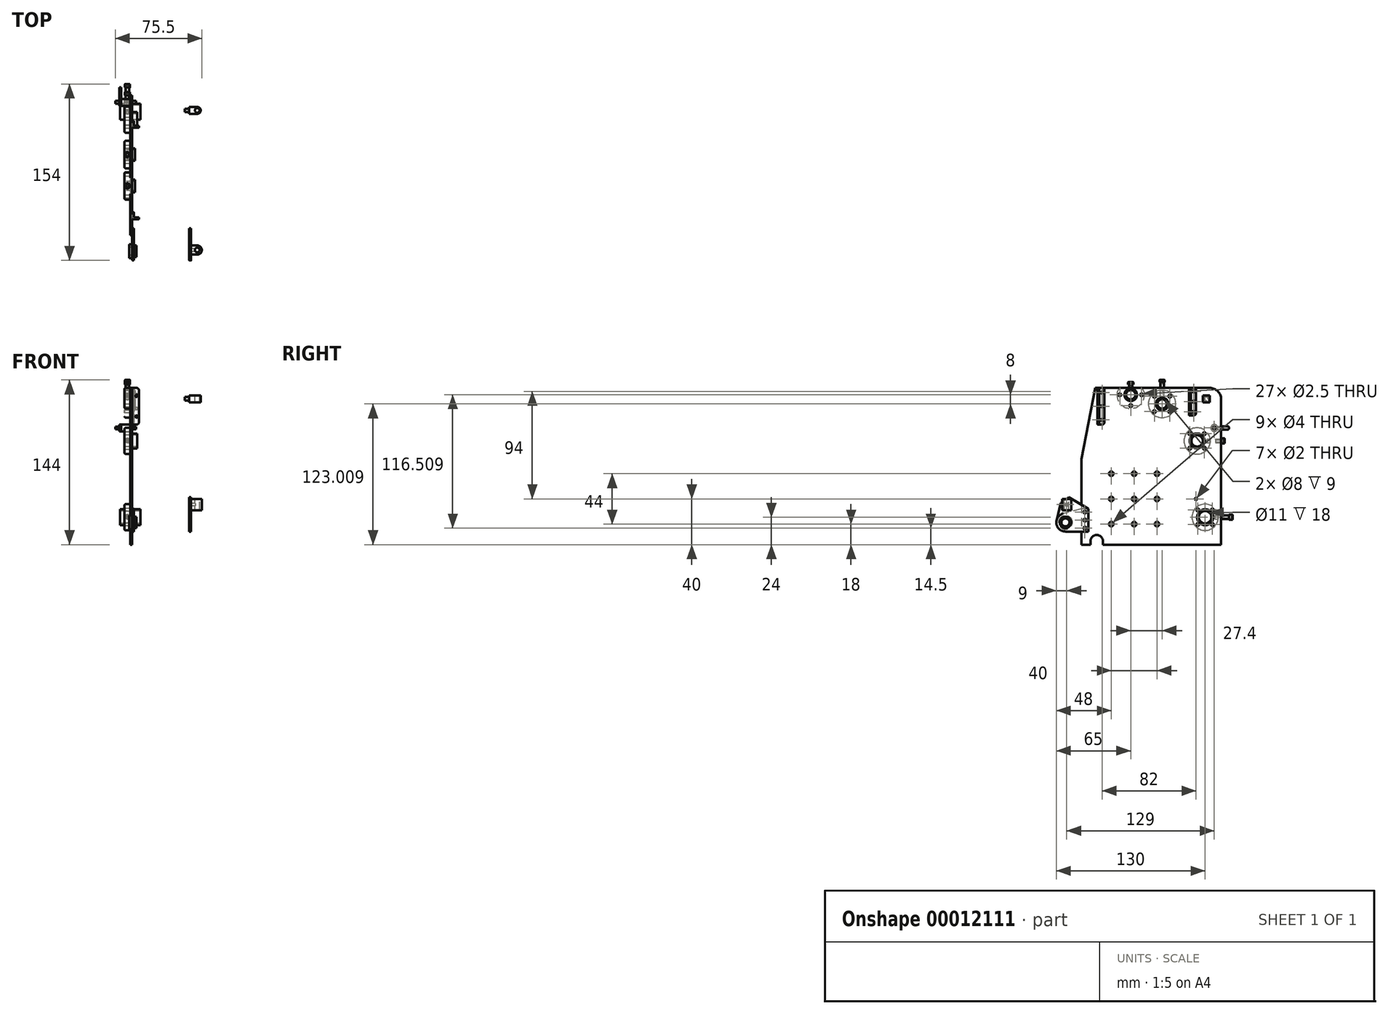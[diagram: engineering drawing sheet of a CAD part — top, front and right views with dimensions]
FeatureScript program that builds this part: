
annotation { "Feature Type Name" : "Feature", "Feature Type Description" : "" }
export const myFeature = defineFeature(function(context is Context, id is Id, definition is map)
    precondition{}
    {
        {
            var Q0;
            Q0=qCreatedBy(makeId("Right.planeOp"),FACE);
            var sketch = newSketch(context, id + "F0", { "sketchPlane" : qUnion([Q0])});
            skLineSegment(sketch, "E0", {"start": v(0, 75) * mm, "end": v(0, 0) * mm});
            skLineSegment(sketch, "E1", {"start": v(0, 0) * mm, "end": v(122, 0) * mm});
            skLineSegment(sketch, "E2", {"start": v(122, 0) * mm, "end": v(122, 127) * mm});
            skLineSegment(sketch, "E3", {"start": v(112, 137) * mm, "end": v(12, 137) * mm});
            skLineSegment(sketch, "E4", {"start": v(12, 137) * mm, "end": v(0, 75) * mm});
            skLineSegment(sketch, "E5", {"start": v(13.3, 0) * mm, "end": v(13.3, 3) * mm, "construction": true});
            skLineSegment(sketch, "E6", {"start": v(108, 0) * mm, "end": v(108, 24) * mm, "construction": true});
            skLineSegment(sketch, "E7", {"start": v(101, 0) * mm, "end": v(101, 90.7) * mm, "construction": true});
            skLineSegment(sketch, "E8", {"start": v(122, 40) * mm, "end": v(100, 40) * mm, "construction": true});
            skLineSegment(sketch, "E9", {"start": v(109, 137) * mm, "end": v(109, 127.5) * mm, "construction": true});
            skLineSegment(sketch, "E10", {"start": v(98, 137) * mm, "end": v(98, 134) * mm, "construction": true});
            skLineSegment(sketch, "E11", {"start": v(70.4, 137) * mm, "end": v(70.4, 101.73) * mm, "construction": true});
            skLineSegment(sketch, "E12", {"start": v(43, 137) * mm, "end": v(43, 131) * mm, "construction": true});
            skLineSegment(sketch, "E13", {"start": v(18, 137) * mm, "end": v(18, 133) * mm, "construction": true});
            skCircle(sketch, "E14", {"center": v(101, 90.7) * mm, "radius": 44.5 * mm, "construction": true});
            skCircle(sketch, "E15", {"center": v(70.4, 123) * mm, "radius": 5.5 * mm});
            skLineSegment(sketch, "E16", {"start": v(70.4, 123) * mm, "end": v(53.04, 123) * mm, "construction": true});
            skCircle(sketch, "E17", {"center": v(43, 131) * mm, "radius": 5.5 * mm});
            skCircle(sketch, "E18", {"center": v(101, 90.7) * mm, "radius": 6.5 * mm});
            skCircle(sketch, "E19", {"center": v(13.3, 3) * mm, "radius": 5.5 * mm});
            skCircle(sketch, "E20", {"center": v(108, 24) * mm, "radius": 7 * mm});
            skCircle(sketch, "E21", {"center": v(18, 133) * mm, "radius": 1 * mm});
            skCircle(sketch, "E22", {"center": v(98, 134) * mm, "radius": 1 * mm});
            skCircle(sketch, "E23", {"center": v(109, 127.5) * mm, "radius": 1.5 * mm});
            skCircle(sketch, "E24", {"center": v(100, 40) * mm, "radius": 1 * mm});
            skCircle(sketch, "E25.0.1.0", {"center": v(18, 121) * mm, "radius": 1 * mm});
            skCircle(sketch, "E25.0.2.0", {"center": v(18, 109) * mm, "radius": 1 * mm});
            skLineSegment(sketch, "E25.direction1", {"start": v(18, 133) * mm, "end": v(6, 133) * mm, "construction": true});
            skLineSegment(sketch, "E25.direction2", {"start": v(18, 133) * mm, "end": v(18, 121) * mm, "construction": true});
            skCircle(sketch, "E26.0.1.0", {"center": v(98, 125) * mm, "radius": 1 * mm});
            skCircle(sketch, "E26.0.2.0", {"center": v(98, 116) * mm, "radius": 1 * mm});
            skLineSegment(sketch, "E26.direction1", {"start": v(98, 134) * mm, "end": v(123, 134) * mm, "construction": true});
            skLineSegment(sketch, "E26.direction2", {"start": v(98, 134) * mm, "end": v(98, 125) * mm, "construction": true});
            skLineSegment(sketch, "E27", {"start": v(122, 102) * mm, "end": v(116, 102) * mm, "construction": true});
            skCircle(sketch, "E28", {"center": v(116, 102) * mm, "radius": 1.25 * mm});
            skLineSegment(sketch, "E29", {"start": v(43, 131) * mm, "end": v(33.5, 131) * mm, "construction": true});
            skCircle(sketch, "E30", {"center": v(33.5, 131) * mm, "radius": 1.25 * mm});
            skLineSegment(sketch, "E31", {"start": v(70.4, 123) * mm, "end": v(63.68, 129.73) * mm, "construction": true});
            skCircle(sketch, "E32", {"center": v(63.68, 129.73) * mm, "radius": 1.25 * mm});
            skCircle(sketch, "E33.1.0", {"center": v(63.68, 116.3) * mm, "radius": 1.25 * mm});
            skCircle(sketch, "E33.2.0", {"center": v(77.12, 116.3) * mm, "radius": 1.25 * mm});
            skCircle(sketch, "E33.3.0", {"center": v(77.12, 129.73) * mm, "radius": 1.25 * mm});
            skLineSegment(sketch, "E34", {"start": v(101, 90.7) * mm, "end": v(94.64, 84.34) * mm, "construction": true});
            skCircle(sketch, "E35", {"center": v(94.64, 84.34) * mm, "radius": 1.25 * mm});
            skCircle(sketch, "E36.1.0", {"center": v(107.36, 84.34) * mm, "radius": 1.25 * mm});
            skCircle(sketch, "E36.2.0", {"center": v(107.36, 97.06) * mm, "radius": 1.25 * mm});
            skCircle(sketch, "E36.3.0", {"center": v(94.64, 97.06) * mm, "radius": 1.25 * mm});
            skLineSegment(sketch, "E37", {"start": v(108, 24) * mm, "end": v(114.36, 17.64) * mm, "construction": true});
            skCircle(sketch, "E38", {"center": v(114.36, 17.64) * mm, "radius": 1.25 * mm});
            skCircle(sketch, "E39.1.0", {"center": v(114.36, 30.36) * mm, "radius": 1.25 * mm});
            skCircle(sketch, "E39.2.0", {"center": v(101.64, 30.36) * mm, "radius": 1.25 * mm});
            skCircle(sketch, "E39.3.0", {"center": v(101.64, 17.64) * mm, "radius": 1.25 * mm});
            skLineSegment(sketch, "E40", {"start": v(7.8, 3) * mm, "end": v(7.8, 0) * mm});
            skLineSegment(sketch, "E41", {"start": v(18.8, 3) * mm, "end": v(18.8, 0) * mm});
            skLineSegment(sketch, "E42", {"start": v(66, 0) * mm, "end": v(66, 18) * mm, "construction": true});
            skCircle(sketch, "E43", {"center": v(66, 18) * mm, "radius": 2 * mm});
            skCircle(sketch, "E44.0.1.0", {"center": v(66, 40) * mm, "radius": 2 * mm});
            skCircle(sketch, "E44.0.2.0", {"center": v(66, 62) * mm, "radius": 2 * mm});
            skCircle(sketch, "E44.1.0.0", {"center": v(46, 18) * mm, "radius": 2 * mm});
            skCircle(sketch, "E44.1.1.0", {"center": v(46, 40) * mm, "radius": 2 * mm});
            skCircle(sketch, "E44.1.2.0", {"center": v(46, 62) * mm, "radius": 2 * mm});
            skCircle(sketch, "E44.2.0.0", {"center": v(26, 18) * mm, "radius": 2 * mm});
            skCircle(sketch, "E44.2.1.0", {"center": v(26, 40) * mm, "radius": 2 * mm});
            skCircle(sketch, "E44.2.2.0", {"center": v(26, 62) * mm, "radius": 2 * mm});
            skLineSegment(sketch, "E44.direction1", {"start": v(66, 18) * mm, "end": v(46, 18) * mm, "construction": true});
            skLineSegment(sketch, "E44.direction2", {"start": v(66, 18) * mm, "end": v(66, 40) * mm, "construction": true});
            skLineSegment(sketch, "E45", {"start": v(0, 14.5) * mm, "end": v(3, 14.5) * mm, "construction": true});
            skCircle(sketch, "E46", {"center": v(3, 14.5) * mm, "radius": 1.25 * mm});
            skCircle(sketch, "E47.0.1.0", {"center": v(3, 21.5) * mm, "radius": 1.25 * mm});
            skCircle(sketch, "E47.0.2.0", {"center": v(3, 28.5) * mm, "radius": 1.25 * mm});
            skLineSegment(sketch, "E47.direction1", {"start": v(3, 14.5) * mm, "end": v(3, 14.5) * mm});
            skLineSegment(sketch, "E47.direction2", {"start": v(3, 14.5) * mm, "end": v(3, 21.5) * mm, "construction": true});
            skPoint(sketch, "E48.visualSharp", {"position": v(122, 137) * mm});
            skArc(sketch, "E48.filletArc", {"start": v(122, 127) * mm, "mid": v(119.07, 134.07) * mm, "end": v(112, 137) * mm});
            skCircle(sketch, "E49.1.0", {"center": v(43, 121.5) * mm, "radius": 1.25 * mm});
            skCircle(sketch, "E49.2.0", {"center": v(52.5, 131) * mm, "radius": 1.25 * mm});
            skCircle(sketch, "E49.3.0", {"center": v(43, 140.5) * mm, "radius": 1.25 * mm});
            skSolve(sketch);
        }
        {
            var Q0;
            {var subQ2=sQuery(id+"F0.wireOp",EDGE,"E0");Q0=makeQuery(id+"F0.imprint","IMPRINT",FACE,{"disambiguationData":[TD([[makeQuery(id+"F0.imprint","IMPRINT",EDGE,{"derivedFrom":subQ2}),1.0]])]});}
            extrude(context, id + "F1", {"entities" : qUnion([Q0]), "depth" : 1.5 * mm});
        }
        {
            var Q0;
            Q0=makeQuery(id+"F1.opExtrude","CAP_FACE",FACE,{"disambiguationData":[OSD([sQuery(id+"F0.wireOp",EDGE,"E0"),sQuery(id+"F0.wireOp",EDGE,"E1"),sQuery(id+"F0.wireOp",EDGE,"E2"),sQuery(id+"F0.wireOp",EDGE,"E3"),sQuery(id+"F0.wireOp",EDGE,"E4"),sQuery(id+"F0.wireOp",EDGE,"E15"),sQuery(id+"F0.wireOp",EDGE,"E17"),sQuery(id+"F0.wireOp",EDGE,"E18"),sQuery(id+"F0.wireOp",EDGE,"E19"),sQuery(id+"F0.wireOp",EDGE,"E20"),sQuery(id+"F0.wireOp",EDGE,"E21"),sQuery(id+"F0.wireOp",EDGE,"E22"),sQuery(id+"F0.wireOp",EDGE,"E23"),sQuery(id+"F0.wireOp",EDGE,"E24"),sQuery(id+"F0.wireOp",EDGE,"E25.0.1.0"),sQuery(id+"F0.wireOp",EDGE,"E25.0.2.0"),sQuery(id+"F0.wireOp",EDGE,"E26.0.1.0"),sQuery(id+"F0.wireOp",EDGE,"E26.0.2.0"),sQuery(id+"F0.wireOp",EDGE,"E28"),sQuery(id+"F0.wireOp",EDGE,"E30"),sQuery(id+"F0.wireOp",EDGE,"E32"),sQuery(id+"F0.wireOp",EDGE,"E33.1.0"),sQuery(id+"F0.wireOp",EDGE,"E33.2.0"),sQuery(id+"F0.wireOp",EDGE,"E33.3.0"),sQuery(id+"F0.wireOp",EDGE,"E35"),sQuery(id+"F0.wireOp",EDGE,"E36.1.0"),sQuery(id+"F0.wireOp",EDGE,"E36.2.0"),sQuery(id+"F0.wireOp",EDGE,"E36.3.0"),sQuery(id+"F0.wireOp",EDGE,"E38"),sQuery(id+"F0.wireOp",EDGE,"E39.1.0"),sQuery(id+"F0.wireOp",EDGE,"E39.2.0"),sQuery(id+"F0.wireOp",EDGE,"E39.3.0"),sQuery(id+"F0.wireOp",EDGE,"E40"),sQuery(id+"F0.wireOp",EDGE,"E41"),sQuery(id+"F0.wireOp",EDGE,"E43"),sQuery(id+"F0.wireOp",EDGE,"E44.0.1.0"),sQuery(id+"F0.wireOp",EDGE,"E44.0.2.0"),sQuery(id+"F0.wireOp",EDGE,"E44.1.0.0"),sQuery(id+"F0.wireOp",EDGE,"E44.1.1.0"),sQuery(id+"F0.wireOp",EDGE,"E44.1.2.0"),sQuery(id+"F0.wireOp",EDGE,"E44.2.0.0"),sQuery(id+"F0.wireOp",EDGE,"E44.2.1.0"),sQuery(id+"F0.wireOp",EDGE,"E44.2.2.0"),sQuery(id+"F0.wireOp",EDGE,"E46"),sQuery(id+"F0.wireOp",EDGE,"E47.0.1.0"),sQuery(id+"F0.wireOp",EDGE,"E47.0.2.0"),sQuery(id+"F0.wireOp",EDGE,"E48.filletArc"),sQuery(id+"F0.wireOp",EDGE,"E49.1.0"),sQuery(id+"F0.wireOp",EDGE,"E49.2.0")])],"isStart":false});
            var sketch = newSketch(context, id + "F2", { "sketchPlane" : qUnion([Q0])});
            skCircle(sketch, "E50.0", {"center": v(18, 133) * mm, "radius": 1 * mm});
            skCircle(sketch, "E50.1", {"center": v(18, 121) * mm, "radius": 1 * mm});
            skCircle(sketch, "E50.2", {"center": v(18, 109) * mm, "radius": 1 * mm});
            skLineSegment(sketch, "E51.bottom", {"start": v(14, 137) * mm, "end": v(18, 137) * mm});
            skLineSegment(sketch, "E51.top", {"start": v(14, 105) * mm, "end": v(18, 105) * mm});
            skLineSegment(sketch, "E51.left", {"start": v(14, 137) * mm, "end": v(14, 105) * mm});
            skLineSegment(sketch, "E51.right", {"start": v(20, 135) * mm, "end": v(20, 107) * mm});
            skLineSegment(sketch, "E52", {"start": v(15.5, 137) * mm, "end": v(15.5, 105) * mm});
            skPoint(sketch, "E53.visualSharp", {"position": v(20, 137) * mm});
            skArc(sketch, "E53.filletArc", {"start": v(20, 135) * mm, "mid": v(19.41, 136.41) * mm, "end": v(18, 137) * mm});
            skPoint(sketch, "E54.visualSharp", {"position": v(20, 105) * mm});
            skArc(sketch, "E54.filletArc", {"start": v(18, 105) * mm, "mid": v(19.41, 105.59) * mm, "end": v(20, 107) * mm});
            skSolve(sketch);
        }
        {
            var Q0;
            {var subQ1=sQuery(id+"F2.wireOp",EDGE,"E51.left");Q0=makeQuery(id+"F2.imprint","IMPRINT",FACE,{"disambiguationData":[TD([[makeQuery(id+"F2.imprint","IMPRINT",EDGE,{"derivedFrom":subQ1}),1.0]])]});}
            extrude(context, id + "F3", {"entities" : qUnion([Q0]), "depth" : 6 * mm});
        }
        {
            var Q0;
            Q0=makeQuery(id+"F2.imprint","IMPRINT",FACE,{"disambiguationData":[TD([[makeQuery(id+"F2.imprint","IMPRINT",EDGE,{"derivedFrom":sQuery(id+"F2.wireOp",EDGE,"E50.0")}),-1.0]])]});
            extrude(context, id + "F4", {"entities" : qUnion([Q0]), "operationType" : NewBodyOperationType.ADD, "depth" : 1.5 * mm});
        }
        {
            var Q0;
            Q0=makeQuery(id+"F3.opExtrude","SWEPT_FACE",FACE,{"disambiguationData":[OSD([sQuery(id+"F2.wireOp",EDGE,"E51.left")])]});
            var sketch = newSketch(context, id + "F5", { "sketchPlane" : qUnion([Q0])});
            skLineSegment(sketch, "E55", {"start": v(5.5, 137) * mm, "end": v(5.5, 105) * mm, "construction": true});
            skLineSegment(sketch, "E56", {"start": v(5.5, 130) * mm, "end": v(7.5, 130) * mm, "construction": true});
            skLineSegment(sketch, "E57", {"start": v(5.5, 112) * mm, "end": v(7.5, 112) * mm, "construction": true});
            skCircle(sketch, "E58", {"center": v(5.5, 130) * mm, "radius": 1 * mm});
            skCircle(sketch, "E59", {"center": v(5.5, 112) * mm, "radius": 1 * mm});
            skSolve(sketch);
        }
        {
            var Q0;
            Q0=makeQuery(id+"F5.imprint","IMPRINT",FACE,{"disambiguationData":[TD([[makeQuery(id+"F5.imprint","IMPRINT",EDGE,{"derivedFrom":sQuery(id+"F5.wireOp",EDGE,"E58")}),1.0]])]});
            var Q1;
            Q1=makeQuery(id+"F5.imprint","IMPRINT",FACE,{"disambiguationData":[TD([[makeQuery(id+"F5.imprint","IMPRINT",EDGE,{"derivedFrom":sQuery(id+"F5.wireOp",EDGE,"E59")}),1.0]])]});
            extrude(context, id + "F6", {"entities" : qUnion([Q0, Q1]), "operationType" : NewBodyOperationType.REMOVE, "oppositeDirection" : true, "depth" : 1.5 * mm});
        }
        {
            var Q0;
            Q0=makeQuery(id+"F3.opExtrude","CAP_EDGE",EDGE,{"disambiguationData":[OSD([sQuery(id+"F2.wireOp",EDGE,"E51.bottom")])],"isStart":false});
            var Q1;
            Q1=makeQuery(id+"F3.opExtrude","CAP_EDGE",EDGE,{"disambiguationData":[OSD([sQuery(id+"F2.wireOp",EDGE,"E51.top")])],"isStart":false});
            fillet(context, id + "F7", {"entities" : qUnion([Q0, Q1]), "radius" : 2 * mm, "tangentPropagation" : true, "allowEdgeOverflow" : false});
        }
        {
            var Q0;
            Q0=makeQuery(id+"F1.opExtrude","CAP_FACE",FACE,{"disambiguationData":[OSD([sQuery(id+"F0.wireOp",EDGE,"E0"),sQuery(id+"F0.wireOp",EDGE,"E1"),sQuery(id+"F0.wireOp",EDGE,"E2"),sQuery(id+"F0.wireOp",EDGE,"E3"),sQuery(id+"F0.wireOp",EDGE,"E4"),sQuery(id+"F0.wireOp",EDGE,"E15"),sQuery(id+"F0.wireOp",EDGE,"E17"),sQuery(id+"F0.wireOp",EDGE,"E18"),sQuery(id+"F0.wireOp",EDGE,"E19"),sQuery(id+"F0.wireOp",EDGE,"E20"),sQuery(id+"F0.wireOp",EDGE,"E21"),sQuery(id+"F0.wireOp",EDGE,"E22"),sQuery(id+"F0.wireOp",EDGE,"E23"),sQuery(id+"F0.wireOp",EDGE,"E24"),sQuery(id+"F0.wireOp",EDGE,"E25.0.1.0"),sQuery(id+"F0.wireOp",EDGE,"E25.0.2.0"),sQuery(id+"F0.wireOp",EDGE,"E26.0.1.0"),sQuery(id+"F0.wireOp",EDGE,"E26.0.2.0"),sQuery(id+"F0.wireOp",EDGE,"E28"),sQuery(id+"F0.wireOp",EDGE,"E30"),sQuery(id+"F0.wireOp",EDGE,"E32"),sQuery(id+"F0.wireOp",EDGE,"E33.1.0"),sQuery(id+"F0.wireOp",EDGE,"E33.2.0"),sQuery(id+"F0.wireOp",EDGE,"E33.3.0"),sQuery(id+"F0.wireOp",EDGE,"E35"),sQuery(id+"F0.wireOp",EDGE,"E36.1.0"),sQuery(id+"F0.wireOp",EDGE,"E36.2.0"),sQuery(id+"F0.wireOp",EDGE,"E36.3.0"),sQuery(id+"F0.wireOp",EDGE,"E38"),sQuery(id+"F0.wireOp",EDGE,"E39.1.0"),sQuery(id+"F0.wireOp",EDGE,"E39.2.0"),sQuery(id+"F0.wireOp",EDGE,"E39.3.0"),sQuery(id+"F0.wireOp",EDGE,"E40"),sQuery(id+"F0.wireOp",EDGE,"E41"),sQuery(id+"F0.wireOp",EDGE,"E43"),sQuery(id+"F0.wireOp",EDGE,"E44.0.1.0"),sQuery(id+"F0.wireOp",EDGE,"E44.0.2.0"),sQuery(id+"F0.wireOp",EDGE,"E44.1.0.0"),sQuery(id+"F0.wireOp",EDGE,"E44.1.1.0"),sQuery(id+"F0.wireOp",EDGE,"E44.1.2.0"),sQuery(id+"F0.wireOp",EDGE,"E44.2.0.0"),sQuery(id+"F0.wireOp",EDGE,"E44.2.1.0"),sQuery(id+"F0.wireOp",EDGE,"E44.2.2.0"),sQuery(id+"F0.wireOp",EDGE,"E46"),sQuery(id+"F0.wireOp",EDGE,"E47.0.1.0"),sQuery(id+"F0.wireOp",EDGE,"E47.0.2.0"),sQuery(id+"F0.wireOp",EDGE,"E48.filletArc"),sQuery(id+"F0.wireOp",EDGE,"E49.1.0"),sQuery(id+"F0.wireOp",EDGE,"E49.2.0")])],"isStart":false});
            var sketch = newSketch(context, id + "F8", { "sketchPlane" : qUnion([Q0])});
            skCircle(sketch, "E60.0", {"center": v(98, 134) * mm, "radius": 1 * mm});
            skCircle(sketch, "E60.1", {"center": v(98, 125) * mm, "radius": 1 * mm});
            skCircle(sketch, "E60.2", {"center": v(98, 116) * mm, "radius": 1 * mm});
            skLineSegment(sketch, "E61.bottom", {"start": v(98, 137) * mm, "end": v(94, 137) * mm});
            skLineSegment(sketch, "E61.top", {"start": v(98, 113) * mm, "end": v(94, 113) * mm});
            skLineSegment(sketch, "E61.left", {"start": v(100, 135) * mm, "end": v(100, 115) * mm});
            skLineSegment(sketch, "E61.right", {"start": v(94, 137) * mm, "end": v(94, 113) * mm});
            skLineSegment(sketch, "E62", {"start": v(95.5, 137) * mm, "end": v(95.5, 113) * mm});
            skPoint(sketch, "E63.visualSharp", {"position": v(100, 113) * mm});
            skArc(sketch, "E63.filletArc", {"start": v(98, 113) * mm, "mid": v(99.41, 113.59) * mm, "end": v(100, 115) * mm});
            skPoint(sketch, "E64.visualSharp", {"position": v(100, 137) * mm});
            skArc(sketch, "E64.filletArc", {"start": v(100, 135) * mm, "mid": v(99.41, 136.41) * mm, "end": v(98, 137) * mm});
            skSolve(sketch);
        }
        {
            var Q0;
            {var subQ1=sQuery(id+"F8.wireOp",EDGE,"E61.right");Q0=makeQuery(id+"F8.imprint","IMPRINT",FACE,{"disambiguationData":[TD([[makeQuery(id+"F8.imprint","IMPRINT",EDGE,{"derivedFrom":subQ1}),1.0]])]});}
            extrude(context, id + "F9", {"entities" : qUnion([Q0]), "depth" : 6 * mm});
        }
        {
            var Q0;
            Q0=makeQuery(id+"F8.imprint","IMPRINT",FACE,{"disambiguationData":[TD([[makeQuery(id+"F8.imprint","IMPRINT",EDGE,{"derivedFrom":sQuery(id+"F8.wireOp",EDGE,"E60.0")}),-1.0]])]});
            extrude(context, id + "F10", {"entities" : qUnion([Q0]), "operationType" : NewBodyOperationType.ADD, "depth" : 1.5 * mm});
        }
        {
            var Q0;
            Q0=makeQuery(id+"F9.opExtrude","SWEPT_FACE",FACE,{"disambiguationData":[OSD([sQuery(id+"F8.wireOp",EDGE,"E61.right")])]});
            var sketch = newSketch(context, id + "F11", { "sketchPlane" : qUnion([Q0])});
            skLineSegment(sketch, "E65", {"start": v(5.5, 137) * mm, "end": v(5.5, 113) * mm, "construction": true});
            skLineSegment(sketch, "E66", {"start": v(5.5, 131) * mm, "end": v(7.5, 131) * mm, "construction": true});
            skLineSegment(sketch, "E67", {"start": v(5.5, 119) * mm, "end": v(7.5, 119) * mm, "construction": true});
            skCircle(sketch, "E68", {"center": v(5.5, 131) * mm, "radius": 1 * mm});
            skCircle(sketch, "E69", {"center": v(5.5, 119) * mm, "radius": 1 * mm});
            skSolve(sketch);
        }
        {
            var Q0;
            Q0=makeQuery(id+"F11.imprint","IMPRINT",FACE,{"disambiguationData":[TD([[makeQuery(id+"F11.imprint","IMPRINT",EDGE,{"derivedFrom":sQuery(id+"F11.wireOp",EDGE,"E68")}),1.0]])]});
            var Q1;
            Q1=makeQuery(id+"F11.imprint","IMPRINT",FACE,{"disambiguationData":[TD([[makeQuery(id+"F11.imprint","IMPRINT",EDGE,{"derivedFrom":sQuery(id+"F11.wireOp",EDGE,"E69")}),1.0]])]});
            extrude(context, id + "F12", {"entities" : qUnion([Q0, Q1]), "operationType" : NewBodyOperationType.REMOVE, "oppositeDirection" : true, "depth" : 1.5 * mm});
        }
        {
            var Q0;
            Q0=makeQuery(id+"F9.opExtrude","CAP_EDGE",EDGE,{"disambiguationData":[OSD([sQuery(id+"F8.wireOp",EDGE,"E61.bottom")])],"isStart":false});
            var Q1;
            Q1=makeQuery(id+"F9.opExtrude","CAP_EDGE",EDGE,{"disambiguationData":[OSD([sQuery(id+"F8.wireOp",EDGE,"E61.top")])],"isStart":false});
            fillet(context, id + "F13", {"entities" : qUnion([Q0, Q1]), "radius" : 2 * mm, "tangentPropagation" : true, "allowEdgeOverflow" : false});
        }
        {
            var Q0;
            Q0=makeQuery(id+"F1.opExtrude","CAP_FACE",FACE,{"disambiguationData":[OSD([sQuery(id+"F0.wireOp",EDGE,"E0"),sQuery(id+"F0.wireOp",EDGE,"E1"),sQuery(id+"F0.wireOp",EDGE,"E2"),sQuery(id+"F0.wireOp",EDGE,"E3"),sQuery(id+"F0.wireOp",EDGE,"E4"),sQuery(id+"F0.wireOp",EDGE,"E15"),sQuery(id+"F0.wireOp",EDGE,"E17"),sQuery(id+"F0.wireOp",EDGE,"E18"),sQuery(id+"F0.wireOp",EDGE,"E19"),sQuery(id+"F0.wireOp",EDGE,"E20"),sQuery(id+"F0.wireOp",EDGE,"E21"),sQuery(id+"F0.wireOp",EDGE,"E22"),sQuery(id+"F0.wireOp",EDGE,"E23"),sQuery(id+"F0.wireOp",EDGE,"E24"),sQuery(id+"F0.wireOp",EDGE,"E25.0.1.0"),sQuery(id+"F0.wireOp",EDGE,"E25.0.2.0"),sQuery(id+"F0.wireOp",EDGE,"E26.0.1.0"),sQuery(id+"F0.wireOp",EDGE,"E26.0.2.0"),sQuery(id+"F0.wireOp",EDGE,"E28"),sQuery(id+"F0.wireOp",EDGE,"E30"),sQuery(id+"F0.wireOp",EDGE,"E32"),sQuery(id+"F0.wireOp",EDGE,"E33.1.0"),sQuery(id+"F0.wireOp",EDGE,"E33.2.0"),sQuery(id+"F0.wireOp",EDGE,"E33.3.0"),sQuery(id+"F0.wireOp",EDGE,"E35"),sQuery(id+"F0.wireOp",EDGE,"E36.1.0"),sQuery(id+"F0.wireOp",EDGE,"E36.2.0"),sQuery(id+"F0.wireOp",EDGE,"E36.3.0"),sQuery(id+"F0.wireOp",EDGE,"E38"),sQuery(id+"F0.wireOp",EDGE,"E39.1.0"),sQuery(id+"F0.wireOp",EDGE,"E39.2.0"),sQuery(id+"F0.wireOp",EDGE,"E39.3.0"),sQuery(id+"F0.wireOp",EDGE,"E40"),sQuery(id+"F0.wireOp",EDGE,"E41"),sQuery(id+"F0.wireOp",EDGE,"E43"),sQuery(id+"F0.wireOp",EDGE,"E44.0.1.0"),sQuery(id+"F0.wireOp",EDGE,"E44.0.2.0"),sQuery(id+"F0.wireOp",EDGE,"E44.1.0.0"),sQuery(id+"F0.wireOp",EDGE,"E44.1.1.0"),sQuery(id+"F0.wireOp",EDGE,"E44.1.2.0"),sQuery(id+"F0.wireOp",EDGE,"E44.2.0.0"),sQuery(id+"F0.wireOp",EDGE,"E44.2.1.0"),sQuery(id+"F0.wireOp",EDGE,"E44.2.2.0"),sQuery(id+"F0.wireOp",EDGE,"E46"),sQuery(id+"F0.wireOp",EDGE,"E47.0.1.0"),sQuery(id+"F0.wireOp",EDGE,"E47.0.2.0"),sQuery(id+"F0.wireOp",EDGE,"E48.filletArc"),sQuery(id+"F0.wireOp",EDGE,"E49.1.0"),sQuery(id+"F0.wireOp",EDGE,"E49.2.0")])],"isStart":true});
            var sketch = newSketch(context, id + "F14", { "sketchPlane" : qUnion([Q0])});
            skCircle(sketch, "E70.0", {"center": v(-43, 131) * mm, "radius": 5.5 * mm});
            skCircle(sketch, "E70.1", {"center": v(-43, 121.5) * mm, "radius": 1.25 * mm});
            skCircle(sketch, "E70.2", {"center": v(-52.5, 131) * mm, "radius": 1.25 * mm});
            skCircle(sketch, "E70.3", {"center": v(-33.5, 131) * mm, "radius": 1.25 * mm});
            skCircle(sketch, "E71", {"center": v(-43, 131) * mm, "radius": 12 * mm});
            skCircle(sketch, "E72", {"center": v(-43, 131) * mm, "radius": 4 * mm});
            skSolve(sketch);
        }
        {
            var Q0;
            Q0=makeQuery(id+"F14.imprint","IMPRINT",FACE,{"disambiguationData":[TD([[makeQuery(id+"F14.imprint","IMPRINT",EDGE,{"derivedFrom":sQuery(id+"F14.wireOp",EDGE,"E70.0")}),-1.0]])]});
            extrude(context, id + "F15", {"entities" : qUnion([Q0]), "oppositeDirection" : true, "depth" : 4 * mm});
        }
        {
            var Q0;
            Q0=makeQuery(id+"F14.imprint","IMPRINT",FACE,{"disambiguationData":[TD([[makeQuery(id+"F14.imprint","IMPRINT",EDGE,{"derivedFrom":sQuery(id+"F14.wireOp",EDGE,"E70.0")}),1.0]])]});
            var Q1;
            Q1=makeQuery(id+"F14.imprint","IMPRINT",FACE,{"disambiguationData":[TD([[makeQuery(id+"F14.imprint","IMPRINT",EDGE,{"derivedFrom":sQuery(id+"F14.wireOp",EDGE,"E70.0")}),-1.0]])]});
            extrude(context, id + "F16", {"entities" : qUnion([Q0, Q1]), "operationType" : NewBodyOperationType.ADD, "depth" : 5 * mm});
        }
        {
            var Q0;
            Q0=makeQuery(id+"F16.opExtrude","SWEPT_FACE",FACE,{"disambiguationData":[OSD([sQuery(id+"F0.wireOp",EDGE,"E3")])]});
            var sketch = newSketch(context, id + "F17", { "sketchPlane" : qUnion([Q0])});
            skLineSegment(sketch, "E73", {"start": v(-5, 43) * mm, "end": v(0, 43) * mm, "construction": true});
            skCircle(sketch, "E74", {"center": v(-2.5, 43) * mm, "radius": 1.5 * mm});
            skCircle(sketch, "E75", {"center": v(-2.5, 43) * mm, "radius": 0.75 * mm});
            skSolve(sketch);
        }
        {
            var Q0;
            Q0=makeQuery(id+"F17.imprint","IMPRINT",FACE,{"disambiguationData":[TD([[makeQuery(id+"F17.imprint","IMPRINT",EDGE,{"derivedFrom":sQuery(id+"F17.wireOp",EDGE,"E75")}),1.0]])]});
            extrude(context, id + "F18", {"entities" : qUnion([Q0]), "operationType" : NewBodyOperationType.REMOVE, "oppositeDirection" : true, "depth" : 6 * mm});
        }
        {
            var Q0;
            Q0=makeQuery(id+"F17.imprint","IMPRINT",FACE,{"disambiguationData":[TD([[makeQuery(id+"F17.imprint","IMPRINT",EDGE,{"derivedFrom":sQuery(id+"F17.wireOp",EDGE,"E74")}),1.0]])]});
            extrude(context, id + "F19", {"entities" : qUnion([Q0]), "operationType" : NewBodyOperationType.REMOVE, "oppositeDirection" : true, "depth" : 1.5 * mm});
        }
        {
            var Q0;
            {var subQ0=sQuery(id+"F0.wireOp",EDGE,"E3");var subQ1=sQuery(id+"F14.wireOp",EDGE,"E71");Q0=makeQuery(id+"F16.opExtrude","SWEPT_EDGE",EDGE,{"disambiguationData":[OSD([subQ0,subQ1]),TDD([makeQuery(id+"F14.imprint","INTERSECT",VERTEX,{"disambiguationData":[OD(0.0)],"derivedFrom":[makeQuery(id+"F1.opExtrude","CAP_EDGE",EDGE,{"disambiguationData":[OSD([subQ0])],"isStart":true}),subQ1]})])]});}
            var Q1;
            {var subQ0=sQuery(id+"F0.wireOp",EDGE,"E3");var subQ1=sQuery(id+"F14.wireOp",EDGE,"E71");Q1=makeQuery(id+"F16.opExtrude","SWEPT_EDGE",EDGE,{"disambiguationData":[OSD([subQ0,subQ1]),TDD([makeQuery(id+"F14.imprint","INTERSECT",VERTEX,{"disambiguationData":[OD(1.0)],"derivedFrom":[makeQuery(id+"F1.opExtrude","CAP_EDGE",EDGE,{"disambiguationData":[OSD([subQ0])],"isStart":true}),subQ1]})])]});}
            fillet(context, id + "F20", {"entities" : qUnion([Q0, Q1]), "radius" : 5 * mm, "tangentPropagation" : true, "allowEdgeOverflow" : false});
        }
        {
            var Q0;
            Q0=makeQuery(id+"F1.opExtrude","CAP_FACE",FACE,{"disambiguationData":[OSD([sQuery(id+"F0.wireOp",EDGE,"E0"),sQuery(id+"F0.wireOp",EDGE,"E1"),sQuery(id+"F0.wireOp",EDGE,"E2"),sQuery(id+"F0.wireOp",EDGE,"E3"),sQuery(id+"F0.wireOp",EDGE,"E4"),sQuery(id+"F0.wireOp",EDGE,"E15"),sQuery(id+"F0.wireOp",EDGE,"E17"),sQuery(id+"F0.wireOp",EDGE,"E18"),sQuery(id+"F0.wireOp",EDGE,"E19"),sQuery(id+"F0.wireOp",EDGE,"E20"),sQuery(id+"F0.wireOp",EDGE,"E21"),sQuery(id+"F0.wireOp",EDGE,"E22"),sQuery(id+"F0.wireOp",EDGE,"E23"),sQuery(id+"F0.wireOp",EDGE,"E24"),sQuery(id+"F0.wireOp",EDGE,"E25.0.1.0"),sQuery(id+"F0.wireOp",EDGE,"E25.0.2.0"),sQuery(id+"F0.wireOp",EDGE,"E26.0.1.0"),sQuery(id+"F0.wireOp",EDGE,"E26.0.2.0"),sQuery(id+"F0.wireOp",EDGE,"E28"),sQuery(id+"F0.wireOp",EDGE,"E30"),sQuery(id+"F0.wireOp",EDGE,"E32"),sQuery(id+"F0.wireOp",EDGE,"E33.1.0"),sQuery(id+"F0.wireOp",EDGE,"E33.2.0"),sQuery(id+"F0.wireOp",EDGE,"E33.3.0"),sQuery(id+"F0.wireOp",EDGE,"E35"),sQuery(id+"F0.wireOp",EDGE,"E36.1.0"),sQuery(id+"F0.wireOp",EDGE,"E36.2.0"),sQuery(id+"F0.wireOp",EDGE,"E36.3.0"),sQuery(id+"F0.wireOp",EDGE,"E38"),sQuery(id+"F0.wireOp",EDGE,"E39.1.0"),sQuery(id+"F0.wireOp",EDGE,"E39.2.0"),sQuery(id+"F0.wireOp",EDGE,"E39.3.0"),sQuery(id+"F0.wireOp",EDGE,"E40"),sQuery(id+"F0.wireOp",EDGE,"E41"),sQuery(id+"F0.wireOp",EDGE,"E43"),sQuery(id+"F0.wireOp",EDGE,"E44.0.1.0"),sQuery(id+"F0.wireOp",EDGE,"E44.0.2.0"),sQuery(id+"F0.wireOp",EDGE,"E44.1.0.0"),sQuery(id+"F0.wireOp",EDGE,"E44.1.1.0"),sQuery(id+"F0.wireOp",EDGE,"E44.1.2.0"),sQuery(id+"F0.wireOp",EDGE,"E44.2.0.0"),sQuery(id+"F0.wireOp",EDGE,"E44.2.1.0"),sQuery(id+"F0.wireOp",EDGE,"E44.2.2.0"),sQuery(id+"F0.wireOp",EDGE,"E46"),sQuery(id+"F0.wireOp",EDGE,"E47.0.1.0"),sQuery(id+"F0.wireOp",EDGE,"E47.0.2.0"),sQuery(id+"F0.wireOp",EDGE,"E48.filletArc"),sQuery(id+"F0.wireOp",EDGE,"E49.1.0"),sQuery(id+"F0.wireOp",EDGE,"E49.2.0")])],"isStart":true});
            var sketch = newSketch(context, id + "F21", { "sketchPlane" : qUnion([Q0])});
            skCircle(sketch, "E76.0", {"center": v(-77.12, 129.73) * mm, "radius": 1.25 * mm});
            skCircle(sketch, "E76.1", {"center": v(-63.68, 129.73) * mm, "radius": 1.25 * mm});
            skCircle(sketch, "E76.2", {"center": v(-63.68, 116.3) * mm, "radius": 1.25 * mm});
            skCircle(sketch, "E76.3", {"center": v(-77.12, 116.3) * mm, "radius": 1.25 * mm});
            skCircle(sketch, "E76.4", {"center": v(-70.4, 123) * mm, "radius": 5.5 * mm});
            skCircle(sketch, "E77", {"center": v(-70.4, 123) * mm, "radius": 12 * mm});
            skCircle(sketch, "E78", {"center": v(-70.4, 123) * mm, "radius": 4 * mm});
            skSolve(sketch);
        }
        {
            var Q0;
            Q0=makeQuery(id+"F21.imprint","IMPRINT",FACE,{"disambiguationData":[TD([[makeQuery(id+"F21.imprint","IMPRINT",EDGE,{"derivedFrom":sQuery(id+"F21.wireOp",EDGE,"E76.4")}),-1.0]])]});
            extrude(context, id + "F22", {"entities" : qUnion([Q0]), "oppositeDirection" : true, "depth" : 4 * mm});
        }
        {
            var Q0;
            Q0=makeQuery(id+"F21.imprint","IMPRINT",FACE,{"disambiguationData":[TD([[makeQuery(id+"F21.imprint","IMPRINT",EDGE,{"derivedFrom":sQuery(id+"F21.wireOp",EDGE,"E76.0")}),1.0]])]});
            var Q1;
            Q1=makeQuery(id+"F21.imprint","IMPRINT",FACE,{"disambiguationData":[TD([[makeQuery(id+"F21.imprint","IMPRINT",EDGE,{"derivedFrom":sQuery(id+"F21.wireOp",EDGE,"E76.4")}),-1.0]])]});
            extrude(context, id + "F23", {"entities" : qUnion([Q0, Q1]), "operationType" : NewBodyOperationType.ADD, "depth" : 5 * mm});
        }
        {
            var Q0;
            Q0=makeQuery(id+"F1.opExtrude","SWEPT_FACE",FACE,{"disambiguationData":[OSD([sQuery(id+"F0.wireOp",EDGE,"E3")])]});
            var sketch = newSketch(context, id + "F24", { "sketchPlane" : qUnion([Q0])});
            skLineSegment(sketch, "E79.0", {"start": v(-5, 58.4) * mm, "end": v(-5, 82.4) * mm, "construction": true});
            skLineSegment(sketch, "E80", {"start": v(-5, 70.4) * mm, "end": v(0, 70.4) * mm, "construction": true});
            skCircle(sketch, "E81", {"center": v(-2.5, 70.4) * mm, "radius": 1.5 * mm});
            skSolve(sketch);
        }
        {
            var Q0;
            Q0=makeQuery(id+"F24.imprint","IMPRINT",FACE,{"disambiguationData":[TD([[makeQuery(id+"F24.imprint","IMPRINT",EDGE,{"derivedFrom":sQuery(id+"F24.wireOp",EDGE,"E81")}),1.0]])]});
            extrude(context, id + "F25", {"entities" : qUnion([Q0]), "operationType" : NewBodyOperationType.REMOVE, "oppositeDirection" : true, "depth" : 12 * mm});
        }
        {
            var Q0;
            Q0=makeQuery(id+"F1.opExtrude","CAP_FACE",FACE,{"disambiguationData":[OSD([sQuery(id+"F0.wireOp",EDGE,"E0"),sQuery(id+"F0.wireOp",EDGE,"E1"),sQuery(id+"F0.wireOp",EDGE,"E2"),sQuery(id+"F0.wireOp",EDGE,"E3"),sQuery(id+"F0.wireOp",EDGE,"E4"),sQuery(id+"F0.wireOp",EDGE,"E15"),sQuery(id+"F0.wireOp",EDGE,"E17"),sQuery(id+"F0.wireOp",EDGE,"E18"),sQuery(id+"F0.wireOp",EDGE,"E19"),sQuery(id+"F0.wireOp",EDGE,"E20"),sQuery(id+"F0.wireOp",EDGE,"E21"),sQuery(id+"F0.wireOp",EDGE,"E22"),sQuery(id+"F0.wireOp",EDGE,"E23"),sQuery(id+"F0.wireOp",EDGE,"E24"),sQuery(id+"F0.wireOp",EDGE,"E25.0.1.0"),sQuery(id+"F0.wireOp",EDGE,"E25.0.2.0"),sQuery(id+"F0.wireOp",EDGE,"E26.0.1.0"),sQuery(id+"F0.wireOp",EDGE,"E26.0.2.0"),sQuery(id+"F0.wireOp",EDGE,"E28"),sQuery(id+"F0.wireOp",EDGE,"E30"),sQuery(id+"F0.wireOp",EDGE,"E32"),sQuery(id+"F0.wireOp",EDGE,"E33.1.0"),sQuery(id+"F0.wireOp",EDGE,"E33.2.0"),sQuery(id+"F0.wireOp",EDGE,"E33.3.0"),sQuery(id+"F0.wireOp",EDGE,"E35"),sQuery(id+"F0.wireOp",EDGE,"E36.1.0"),sQuery(id+"F0.wireOp",EDGE,"E36.2.0"),sQuery(id+"F0.wireOp",EDGE,"E36.3.0"),sQuery(id+"F0.wireOp",EDGE,"E38"),sQuery(id+"F0.wireOp",EDGE,"E39.1.0"),sQuery(id+"F0.wireOp",EDGE,"E39.2.0"),sQuery(id+"F0.wireOp",EDGE,"E39.3.0"),sQuery(id+"F0.wireOp",EDGE,"E40"),sQuery(id+"F0.wireOp",EDGE,"E41"),sQuery(id+"F0.wireOp",EDGE,"E43"),sQuery(id+"F0.wireOp",EDGE,"E44.0.1.0"),sQuery(id+"F0.wireOp",EDGE,"E44.0.2.0"),sQuery(id+"F0.wireOp",EDGE,"E44.1.0.0"),sQuery(id+"F0.wireOp",EDGE,"E44.1.1.0"),sQuery(id+"F0.wireOp",EDGE,"E44.1.2.0"),sQuery(id+"F0.wireOp",EDGE,"E44.2.0.0"),sQuery(id+"F0.wireOp",EDGE,"E44.2.1.0"),sQuery(id+"F0.wireOp",EDGE,"E44.2.2.0"),sQuery(id+"F0.wireOp",EDGE,"E46"),sQuery(id+"F0.wireOp",EDGE,"E47.0.1.0"),sQuery(id+"F0.wireOp",EDGE,"E47.0.2.0"),sQuery(id+"F0.wireOp",EDGE,"E48.filletArc"),sQuery(id+"F0.wireOp",EDGE,"E49.1.0"),sQuery(id+"F0.wireOp",EDGE,"E49.2.0")])],"isStart":true});
            var sketch = newSketch(context, id + "F26", { "sketchPlane" : qUnion([Q0])});
            skCircle(sketch, "E82.0", {"center": v(-107.36, 84.34) * mm, "radius": 1.25 * mm});
            skCircle(sketch, "E82.1", {"center": v(-107.36, 97.06) * mm, "radius": 1.25 * mm});
            skCircle(sketch, "E82.2", {"center": v(-94.64, 97.06) * mm, "radius": 1.25 * mm});
            skCircle(sketch, "E82.3", {"center": v(-94.64, 84.34) * mm, "radius": 1.25 * mm});
            skCircle(sketch, "E82.4", {"center": v(-101, 90.7) * mm, "radius": 6.5 * mm});
            skCircle(sketch, "E83", {"center": v(-101, 90.7) * mm, "radius": 11.5 * mm});
            skCircle(sketch, "E84", {"center": v(-101, 90.7) * mm, "radius": 5 * mm});
            skSolve(sketch);
        }
        {
            var Q0;
            Q0=makeQuery(id+"F26.imprint","IMPRINT",FACE,{"disambiguationData":[TD([[makeQuery(id+"F26.imprint","IMPRINT",EDGE,{"derivedFrom":sQuery(id+"F26.wireOp",EDGE,"E82.4")}),-1.0]])]});
            extrude(context, id + "F27", {"entities" : qUnion([Q0]), "oppositeDirection" : true, "depth" : 6 * mm});
        }
        {
            var Q0;
            Q0=makeQuery(id+"F26.imprint","IMPRINT",FACE,{"disambiguationData":[TD([[makeQuery(id+"F26.imprint","IMPRINT",EDGE,{"derivedFrom":sQuery(id+"F26.wireOp",EDGE,"E82.0")}),1.0]])]});
            var Q1;
            Q1=makeQuery(id+"F26.imprint","IMPRINT",FACE,{"disambiguationData":[TD([[makeQuery(id+"F26.imprint","IMPRINT",EDGE,{"derivedFrom":sQuery(id+"F26.wireOp",EDGE,"E82.4")}),-1.0]])]});
            extrude(context, id + "F28", {"entities" : qUnion([Q0, Q1]), "operationType" : NewBodyOperationType.ADD, "depth" : 5 * mm});
        }
        {
            var Q0;
            Q0=makeQuery(id+"F1.opExtrude","SWEPT_FACE",FACE,{"disambiguationData":[OSD([sQuery(id+"F0.wireOp",EDGE,"E2")])]});
            var sketch = newSketch(context, id + "F29", { "sketchPlane" : qUnion([Q0])});
            skLineSegment(sketch, "E85.0", {"start": v(5, 102.2) * mm, "end": v(5, 79.2) * mm, "construction": true});
            skLineSegment(sketch, "E86", {"start": v(5, 90.7) * mm, "end": v(0, 90.7) * mm, "construction": true});
            skCircle(sketch, "E87", {"center": v(2.5, 90.7) * mm, "radius": 1.5 * mm});
            skCircle(sketch, "E88", {"center": v(2.5, 90.7) * mm, "radius": 0.75 * mm});
            skSolve(sketch);
        }
        {
            var Q0;
            Q0=makeQuery(id+"F29.imprint","IMPRINT",FACE,{"disambiguationData":[TD([[makeQuery(id+"F29.imprint","IMPRINT",EDGE,{"derivedFrom":sQuery(id+"F29.wireOp",EDGE,"E88")}),1.0]])]});
            extrude(context, id + "F30", {"entities" : qUnion([Q0]), "operationType" : NewBodyOperationType.REMOVE, "oppositeDirection" : true, "depth" : 22 * mm});
        }
        {
            var Q0;
            Q0=makeQuery(id+"F29.imprint","IMPRINT",FACE,{"disambiguationData":[TD([[makeQuery(id+"F29.imprint","IMPRINT",EDGE,{"derivedFrom":sQuery(id+"F29.wireOp",EDGE,"E87")}),1.0]])]});
            extrude(context, id + "F31", {"entities" : qUnion([Q0]), "operationType" : NewBodyOperationType.REMOVE, "oppositeDirection" : true, "depth" : 12.4 * mm});
        }
        {
            var Q0;
            Q0=makeQuery(id+"F1.opExtrude","CAP_FACE",FACE,{"disambiguationData":[OSD([sQuery(id+"F0.wireOp",EDGE,"E0"),sQuery(id+"F0.wireOp",EDGE,"E1"),sQuery(id+"F0.wireOp",EDGE,"E2"),sQuery(id+"F0.wireOp",EDGE,"E3"),sQuery(id+"F0.wireOp",EDGE,"E4"),sQuery(id+"F0.wireOp",EDGE,"E15"),sQuery(id+"F0.wireOp",EDGE,"E17"),sQuery(id+"F0.wireOp",EDGE,"E18"),sQuery(id+"F0.wireOp",EDGE,"E19"),sQuery(id+"F0.wireOp",EDGE,"E20"),sQuery(id+"F0.wireOp",EDGE,"E21"),sQuery(id+"F0.wireOp",EDGE,"E22"),sQuery(id+"F0.wireOp",EDGE,"E23"),sQuery(id+"F0.wireOp",EDGE,"E24"),sQuery(id+"F0.wireOp",EDGE,"E25.0.1.0"),sQuery(id+"F0.wireOp",EDGE,"E25.0.2.0"),sQuery(id+"F0.wireOp",EDGE,"E26.0.1.0"),sQuery(id+"F0.wireOp",EDGE,"E26.0.2.0"),sQuery(id+"F0.wireOp",EDGE,"E28"),sQuery(id+"F0.wireOp",EDGE,"E30"),sQuery(id+"F0.wireOp",EDGE,"E32"),sQuery(id+"F0.wireOp",EDGE,"E33.1.0"),sQuery(id+"F0.wireOp",EDGE,"E33.2.0"),sQuery(id+"F0.wireOp",EDGE,"E33.3.0"),sQuery(id+"F0.wireOp",EDGE,"E35"),sQuery(id+"F0.wireOp",EDGE,"E36.1.0"),sQuery(id+"F0.wireOp",EDGE,"E36.2.0"),sQuery(id+"F0.wireOp",EDGE,"E36.3.0"),sQuery(id+"F0.wireOp",EDGE,"E38"),sQuery(id+"F0.wireOp",EDGE,"E39.1.0"),sQuery(id+"F0.wireOp",EDGE,"E39.2.0"),sQuery(id+"F0.wireOp",EDGE,"E39.3.0"),sQuery(id+"F0.wireOp",EDGE,"E40"),sQuery(id+"F0.wireOp",EDGE,"E41"),sQuery(id+"F0.wireOp",EDGE,"E43"),sQuery(id+"F0.wireOp",EDGE,"E44.0.1.0"),sQuery(id+"F0.wireOp",EDGE,"E44.0.2.0"),sQuery(id+"F0.wireOp",EDGE,"E44.1.0.0"),sQuery(id+"F0.wireOp",EDGE,"E44.1.1.0"),sQuery(id+"F0.wireOp",EDGE,"E44.1.2.0"),sQuery(id+"F0.wireOp",EDGE,"E44.2.0.0"),sQuery(id+"F0.wireOp",EDGE,"E44.2.1.0"),sQuery(id+"F0.wireOp",EDGE,"E44.2.2.0"),sQuery(id+"F0.wireOp",EDGE,"E46"),sQuery(id+"F0.wireOp",EDGE,"E47.0.1.0"),sQuery(id+"F0.wireOp",EDGE,"E47.0.2.0"),sQuery(id+"F0.wireOp",EDGE,"E48.filletArc"),sQuery(id+"F0.wireOp",EDGE,"E49.1.0"),sQuery(id+"F0.wireOp",EDGE,"E49.2.0")])],"isStart":true});
            var sketch = newSketch(context, id + "F32", { "sketchPlane" : qUnion([Q0])});
            skCircle(sketch, "E89.0", {"center": v(-108, 24) * mm, "radius": 7 * mm});
            skCircle(sketch, "E89.1", {"center": v(-114.36, 30.36) * mm, "radius": 1.25 * mm});
            skCircle(sketch, "E89.2", {"center": v(-114.36, 17.64) * mm, "radius": 1.25 * mm});
            skCircle(sketch, "E89.3", {"center": v(-101.64, 17.64) * mm, "radius": 1.25 * mm});
            skCircle(sketch, "E89.4", {"center": v(-101.64, 30.36) * mm, "radius": 1.25 * mm});
            skCircle(sketch, "E90", {"center": v(-108, 24) * mm, "radius": 11.5 * mm});
            skCircle(sketch, "E91", {"center": v(-108, 24) * mm, "radius": 5.5 * mm});
            skSolve(sketch);
        }
        {
            var Q0;
            Q0=makeQuery(id+"F32.imprint","IMPRINT",FACE,{"disambiguationData":[TD([[makeQuery(id+"F32.imprint","IMPRINT",EDGE,{"derivedFrom":sQuery(id+"F32.wireOp",EDGE,"E89.0")}),-1.0]])]});
            extrude(context, id + "F33", {"entities" : qUnion([Q0]), "oppositeDirection" : true, "depth" : 18 * mm, "symmetric" : true});
        }
        {
            var Q0;
            Q0=makeQuery(id+"F32.imprint","IMPRINT",FACE,{"disambiguationData":[TD([[makeQuery(id+"F32.imprint","IMPRINT",EDGE,{"derivedFrom":sQuery(id+"F32.wireOp",EDGE,"E89.0")}),1.0]])]});
            var Q1;
            Q1=makeQuery(id+"F32.imprint","IMPRINT",FACE,{"disambiguationData":[TD([[makeQuery(id+"F32.imprint","IMPRINT",EDGE,{"derivedFrom":sQuery(id+"F32.wireOp",EDGE,"E89.0")}),-1.0]])]});
            extrude(context, id + "F34", {"entities" : qUnion([Q0, Q1]), "operationType" : NewBodyOperationType.ADD, "depth" : 5 * mm});
        }
        {
            var Q0;
            Q0=makeQuery(id+"F1.opExtrude","SWEPT_FACE",FACE,{"disambiguationData":[OSD([sQuery(id+"F0.wireOp",EDGE,"E2")])]});
            var sketch = newSketch(context, id + "F35", { "sketchPlane" : qUnion([Q0])});
            skLineSegment(sketch, "E92.0", {"start": v(5, 35.5) * mm, "end": v(5, 12.5) * mm, "construction": true});
            skLineSegment(sketch, "E93", {"start": v(5, 24) * mm, "end": v(0, 24) * mm, "construction": true});
            skCircle(sketch, "E94", {"center": v(2.5, 24) * mm, "radius": 1.5 * mm});
            skCircle(sketch, "E95", {"center": v(2.5, 24) * mm, "radius": 0.75 * mm});
            skSolve(sketch);
        }
        {
            var Q0;
            Q0=makeQuery(id+"F35.imprint","IMPRINT",FACE,{"disambiguationData":[TD([[makeQuery(id+"F35.imprint","IMPRINT",EDGE,{"derivedFrom":sQuery(id+"F35.wireOp",EDGE,"E95")}),1.0]])]});
            extrude(context, id + "F36", {"entities" : qUnion([Q0]), "operationType" : NewBodyOperationType.REMOVE, "oppositeDirection" : true, "depth" : 10 * mm});
        }
        {
            var Q0;
            Q0=makeQuery(id+"F35.imprint","IMPRINT",FACE,{"disambiguationData":[TD([[makeQuery(id+"F35.imprint","IMPRINT",EDGE,{"derivedFrom":sQuery(id+"F35.wireOp",EDGE,"E94")}),1.0]])]});
            extrude(context, id + "F37", {"entities" : qUnion([Q0]), "operationType" : NewBodyOperationType.REMOVE, "oppositeDirection" : true, "depth" : 5.4 * mm});
        }
        {
            var Q0;
            Q0=makeQuery(id+"F16.opExtrude","CAP_EDGE",EDGE,{"disambiguationData":[OSD([sQuery(id+"F14.wireOp",EDGE,"E71")])],"isStart":false});
            var Q1;
            Q1=makeQuery(id+"F23.opExtrude","CAP_EDGE",EDGE,{"disambiguationData":[OSD([sQuery(id+"F21.wireOp",EDGE,"E77")])],"isStart":false});
            var Q2;
            Q2=makeQuery(id+"F28.opExtrude","CAP_EDGE",EDGE,{"disambiguationData":[OSD([sQuery(id+"F26.wireOp",EDGE,"E83")])],"isStart":false});
            var Q3;
            Q3=makeQuery(id+"F34.opExtrude","CAP_EDGE",EDGE,{"disambiguationData":[OSD([sQuery(id+"F32.wireOp",EDGE,"E90")])],"isStart":false});
            fillet(context, id + "F38", {"entities" : qUnion([Q0, Q1, Q2, Q3]), "radius" : 1 * mm, "tangentPropagation" : true, "allowEdgeOverflow" : false});
        }
        {
            var Q0;
            Q0=makeQuery(id+"F1.opExtrude","CAP_FACE",FACE,{"disambiguationData":[OSD([sQuery(id+"F0.wireOp",EDGE,"E0"),sQuery(id+"F0.wireOp",EDGE,"E1"),sQuery(id+"F0.wireOp",EDGE,"E2"),sQuery(id+"F0.wireOp",EDGE,"E3"),sQuery(id+"F0.wireOp",EDGE,"E4"),sQuery(id+"F0.wireOp",EDGE,"E15"),sQuery(id+"F0.wireOp",EDGE,"E17"),sQuery(id+"F0.wireOp",EDGE,"E18"),sQuery(id+"F0.wireOp",EDGE,"E19"),sQuery(id+"F0.wireOp",EDGE,"E20"),sQuery(id+"F0.wireOp",EDGE,"E21"),sQuery(id+"F0.wireOp",EDGE,"E22"),sQuery(id+"F0.wireOp",EDGE,"E23"),sQuery(id+"F0.wireOp",EDGE,"E24"),sQuery(id+"F0.wireOp",EDGE,"E25.0.1.0"),sQuery(id+"F0.wireOp",EDGE,"E25.0.2.0"),sQuery(id+"F0.wireOp",EDGE,"E26.0.1.0"),sQuery(id+"F0.wireOp",EDGE,"E26.0.2.0"),sQuery(id+"F0.wireOp",EDGE,"E28"),sQuery(id+"F0.wireOp",EDGE,"E30"),sQuery(id+"F0.wireOp",EDGE,"E32"),sQuery(id+"F0.wireOp",EDGE,"E33.1.0"),sQuery(id+"F0.wireOp",EDGE,"E33.2.0"),sQuery(id+"F0.wireOp",EDGE,"E33.3.0"),sQuery(id+"F0.wireOp",EDGE,"E35"),sQuery(id+"F0.wireOp",EDGE,"E36.1.0"),sQuery(id+"F0.wireOp",EDGE,"E36.2.0"),sQuery(id+"F0.wireOp",EDGE,"E36.3.0"),sQuery(id+"F0.wireOp",EDGE,"E38"),sQuery(id+"F0.wireOp",EDGE,"E39.1.0"),sQuery(id+"F0.wireOp",EDGE,"E39.2.0"),sQuery(id+"F0.wireOp",EDGE,"E39.3.0"),sQuery(id+"F0.wireOp",EDGE,"E40"),sQuery(id+"F0.wireOp",EDGE,"E41"),sQuery(id+"F0.wireOp",EDGE,"E43"),sQuery(id+"F0.wireOp",EDGE,"E44.0.1.0"),sQuery(id+"F0.wireOp",EDGE,"E44.0.2.0"),sQuery(id+"F0.wireOp",EDGE,"E44.1.0.0"),sQuery(id+"F0.wireOp",EDGE,"E44.1.1.0"),sQuery(id+"F0.wireOp",EDGE,"E44.1.2.0"),sQuery(id+"F0.wireOp",EDGE,"E44.2.0.0"),sQuery(id+"F0.wireOp",EDGE,"E44.2.1.0"),sQuery(id+"F0.wireOp",EDGE,"E44.2.2.0"),sQuery(id+"F0.wireOp",EDGE,"E46"),sQuery(id+"F0.wireOp",EDGE,"E47.0.1.0"),sQuery(id+"F0.wireOp",EDGE,"E47.0.2.0"),sQuery(id+"F0.wireOp",EDGE,"E48.filletArc"),sQuery(id+"F0.wireOp",EDGE,"E49.1.0"),sQuery(id+"F0.wireOp",EDGE,"E49.2.0")])],"isStart":false});
            var sketch = newSketch(context, id + "F39", { "sketchPlane" : qUnion([Q0])});
            skCircle(sketch, "E96.0", {"center": v(3, 28.5) * mm, "radius": 1.25 * mm});
            skCircle(sketch, "E96.1", {"center": v(3, 21.5) * mm, "radius": 1.25 * mm});
            skCircle(sketch, "E96.2", {"center": v(3, 14.5) * mm, "radius": 1.25 * mm});
            skLineSegment(sketch, "E97", {"start": v(6, 31.5) * mm, "end": v(0, 31.5) * mm});
            skLineSegment(sketch, "E98", {"start": v(6, 31.5) * mm, "end": v(6, 11.5) * mm});
            skLineSegment(sketch, "E99", {"start": v(6, 11.5) * mm, "end": v(-14, 11.5) * mm});
            skLineSegment(sketch, "E100", {"start": v(-14, 11.5) * mm, "end": v(-14, 19.5) * mm, "construction": true});
            skCircle(sketch, "E101", {"center": v(-14, 19.5) * mm, "radius": 8 * mm});
            skLineSegment(sketch, "E102", {"start": v(0, 31.5) * mm, "end": v(-16.06, 27.23) * mm});
            skCircle(sketch, "E103", {"center": v(-14, 19.5) * mm, "radius": 6 * mm});
            skCircle(sketch, "E104", {"center": v(-14, 19.5) * mm, "radius": 5 * mm});
            skCircle(sketch, "E105", {"center": v(-14, 19.5) * mm, "radius": 3.5 * mm});
            skSolve(sketch);
        }
        {
            var Q0;
            Q0=makeQuery(id+"F39.imprint","IMPRINT",FACE,{"disambiguationData":[TD([[makeQuery(id+"F39.imprint","IMPRINT",EDGE,{"derivedFrom":sQuery(id+"F39.wireOp",EDGE,"E96.0")}),-1.0]])]});
            var Q1;
            {var subQ3=sQuery(id+"F39.wireOp",EDGE,"E102");Q1=makeQuery(id+"F39.imprint","IMPRINT",FACE,{"disambiguationData":[TD([[makeQuery(id+"F39.imprint","IMPRINT",EDGE,{"derivedFrom":subQ3}),1.0]])]});}
            var Q2;
            Q2=makeQuery(id+"F39.imprint","IMPRINT",FACE,{"disambiguationData":[TD([[makeQuery(id+"F39.imprint","IMPRINT",EDGE,{"derivedFrom":sQuery(id+"F39.wireOp",EDGE,"E103")}),-1.0]])]});
            var Q3;
            Q3=makeQuery(id+"F39.imprint","IMPRINT",FACE,{"disambiguationData":[TD([[makeQuery(id+"F39.imprint","IMPRINT",EDGE,{"derivedFrom":sQuery(id+"F39.wireOp",EDGE,"E103")}),1.0]])]});
            extrude(context, id + "F40", {"entities" : qUnion([Q0, Q1, Q2, Q3]), "depth" : 1.5 * mm});
        }
        {
            var Q0;
            Q0=makeQuery(id+"F39.imprint","IMPRINT",FACE,{"disambiguationData":[TD([[makeQuery(id+"F39.imprint","IMPRINT",EDGE,{"derivedFrom":sQuery(id+"F39.wireOp",EDGE,"E104")}),1.0]])]});
            extrude(context, id + "F41", {"entities" : qUnion([Q0]), "depth" : 4 * mm});
        }
        {
            var Q0;
            Q0=makeQuery(id+"F39.imprint","IMPRINT",FACE,{"disambiguationData":[TD([[makeQuery(id+"F39.imprint","IMPRINT",EDGE,{"derivedFrom":sQuery(id+"F39.wireOp",EDGE,"E103")}),1.0]])]});
            var Q1;
            Q1=makeQuery(id+"F39.imprint","IMPRINT",FACE,{"disambiguationData":[TD([[makeQuery(id+"F39.imprint","IMPRINT",EDGE,{"derivedFrom":sQuery(id+"F39.wireOp",EDGE,"E104")}),1.0]])]});
            extrude(context, id + "F42", {"entities" : qUnion([Q0, Q1]), "operationType" : NewBodyOperationType.ADD, "oppositeDirection" : true, "depth" : 2.5 * mm});
        }
        {
            var Q0;
            Q0=makeQuery(id+"F1.opExtrude","CAP_FACE",FACE,{"disambiguationData":[OSD([sQuery(id+"F0.wireOp",EDGE,"E0"),sQuery(id+"F0.wireOp",EDGE,"E1"),sQuery(id+"F0.wireOp",EDGE,"E2"),sQuery(id+"F0.wireOp",EDGE,"E3"),sQuery(id+"F0.wireOp",EDGE,"E4"),sQuery(id+"F0.wireOp",EDGE,"E15"),sQuery(id+"F0.wireOp",EDGE,"E17"),sQuery(id+"F0.wireOp",EDGE,"E18"),sQuery(id+"F0.wireOp",EDGE,"E19"),sQuery(id+"F0.wireOp",EDGE,"E20"),sQuery(id+"F0.wireOp",EDGE,"E21"),sQuery(id+"F0.wireOp",EDGE,"E22"),sQuery(id+"F0.wireOp",EDGE,"E23"),sQuery(id+"F0.wireOp",EDGE,"E24"),sQuery(id+"F0.wireOp",EDGE,"E25.0.1.0"),sQuery(id+"F0.wireOp",EDGE,"E25.0.2.0"),sQuery(id+"F0.wireOp",EDGE,"E26.0.1.0"),sQuery(id+"F0.wireOp",EDGE,"E26.0.2.0"),sQuery(id+"F0.wireOp",EDGE,"E28"),sQuery(id+"F0.wireOp",EDGE,"E30"),sQuery(id+"F0.wireOp",EDGE,"E32"),sQuery(id+"F0.wireOp",EDGE,"E33.1.0"),sQuery(id+"F0.wireOp",EDGE,"E33.2.0"),sQuery(id+"F0.wireOp",EDGE,"E33.3.0"),sQuery(id+"F0.wireOp",EDGE,"E35"),sQuery(id+"F0.wireOp",EDGE,"E36.1.0"),sQuery(id+"F0.wireOp",EDGE,"E36.2.0"),sQuery(id+"F0.wireOp",EDGE,"E36.3.0"),sQuery(id+"F0.wireOp",EDGE,"E38"),sQuery(id+"F0.wireOp",EDGE,"E39.1.0"),sQuery(id+"F0.wireOp",EDGE,"E39.2.0"),sQuery(id+"F0.wireOp",EDGE,"E39.3.0"),sQuery(id+"F0.wireOp",EDGE,"E40"),sQuery(id+"F0.wireOp",EDGE,"E41"),sQuery(id+"F0.wireOp",EDGE,"E43"),sQuery(id+"F0.wireOp",EDGE,"E44.0.1.0"),sQuery(id+"F0.wireOp",EDGE,"E44.0.2.0"),sQuery(id+"F0.wireOp",EDGE,"E44.1.0.0"),sQuery(id+"F0.wireOp",EDGE,"E44.1.1.0"),sQuery(id+"F0.wireOp",EDGE,"E44.1.2.0"),sQuery(id+"F0.wireOp",EDGE,"E44.2.0.0"),sQuery(id+"F0.wireOp",EDGE,"E44.2.1.0"),sQuery(id+"F0.wireOp",EDGE,"E44.2.2.0"),sQuery(id+"F0.wireOp",EDGE,"E46"),sQuery(id+"F0.wireOp",EDGE,"E47.0.1.0"),sQuery(id+"F0.wireOp",EDGE,"E47.0.2.0"),sQuery(id+"F0.wireOp",EDGE,"E48.filletArc"),sQuery(id+"F0.wireOp",EDGE,"E49.1.0"),sQuery(id+"F0.wireOp",EDGE,"E49.2.0")])],"isStart":false});
            cPlane(context, id + "F43", {"entities" : qUnion([Q0]), "cplaneType" : CPlaneType.OFFSET, "offset" : 50 * mm, "width" : 150 * mm, "height" : 150 * mm});
        }
        {
            var Q0;
            Q0=qCreatedBy(id+"F43.planeOp",FACE);
            var sketch = newSketch(context, id + "F44", { "sketchPlane" : qUnion([Q0])});
            skCircle(sketch, "E106.0", {"center": v(3, 28.5) * mm, "radius": 1.25 * mm});
            skCircle(sketch, "E106.1", {"center": v(3, 21.5) * mm, "radius": 1.25 * mm});
            skCircle(sketch, "E106.2", {"center": v(3, 14.5) * mm, "radius": 1.25 * mm});
            skCircle(sketch, "E106.3", {"center": v(-14, 19.5) * mm, "radius": 3.5 * mm});
            skCircle(sketch, "E106.4", {"center": v(-14, 19.5) * mm, "radius": 5 * mm});
            skCircle(sketch, "E106.5", {"center": v(-14, 19.5) * mm, "radius": 6 * mm});
            skCircle(sketch, "E107.0", {"center": v(-14, 19.5) * mm, "radius": 8 * mm});
            skLineSegment(sketch, "E108", {"start": v(-14, 11.5) * mm, "end": v(6, 11.5) * mm});
            skLineSegment(sketch, "E109", {"start": v(6, 11.5) * mm, "end": v(6, 31.5) * mm});
            skLineSegment(sketch, "E110", {"start": v(6, 31.5) * mm, "end": v(-11, 41.5) * mm});
            skLineSegment(sketch, "E111", {"start": v(-11, 41.5) * mm, "end": v(-18, 36.5) * mm});
            skLineSegment(sketch, "E112", {"start": v(-18, 36.5) * mm, "end": v(-21.76, 21.44) * mm});
            skLineSegment(sketch, "E113", {"start": v(-14, 19.5) * mm, "end": v(-14, 35) * mm, "construction": true});
            skLineSegment(sketch, "E114", {"start": v(-14, 35) * mm, "end": v(-13, 35) * mm, "construction": true});
            skCircle(sketch, "E115", {"center": v(-13, 35) * mm, "radius": 1.25 * mm});
            skSolve(sketch);
        }
        {
            var Q0;
            Q0=makeQuery(id+"F44.imprint","IMPRINT",FACE,{"disambiguationData":[TD([[makeQuery(id+"F44.imprint","IMPRINT",EDGE,{"derivedFrom":sQuery(id+"F44.wireOp",EDGE,"E106.0")}),-1.0]])]});
            var Q1;
            Q1=makeQuery(id+"F44.imprint","IMPRINT",FACE,{"disambiguationData":[TD([[makeQuery(id+"F44.imprint","IMPRINT",EDGE,{"derivedFrom":sQuery(id+"F44.wireOp",EDGE,"E106.5")}),-1.0]])]});
            var Q2;
            Q2=makeQuery(id+"F44.imprint","IMPRINT",FACE,{"disambiguationData":[TD([[makeQuery(id+"F44.imprint","IMPRINT",EDGE,{"derivedFrom":sQuery(id+"F44.wireOp",EDGE,"E106.4")}),-1.0]])]});
            extrude(context, id + "F45", {"entities" : qUnion([Q0, Q1, Q2]), "depth" : 1.5 * mm});
        }
        {
            var Q0;
            Q0=makeQuery(id+"F45.opExtrude","CAP_FACE",FACE,{"disambiguationData":[OSD([sQuery(id+"F44.wireOp",EDGE,"E106.0"),sQuery(id+"F44.wireOp",EDGE,"E106.1"),sQuery(id+"F44.wireOp",EDGE,"E106.2"),sQuery(id+"F44.wireOp",EDGE,"E106.4"),sQuery(id+"F44.wireOp",EDGE,"E107.0"),sQuery(id+"F44.wireOp",EDGE,"E108"),sQuery(id+"F44.wireOp",EDGE,"E109"),sQuery(id+"F44.wireOp",EDGE,"E110"),sQuery(id+"F44.wireOp",EDGE,"E111"),sQuery(id+"F44.wireOp",EDGE,"E112"),sQuery(id+"F44.wireOp",EDGE,"E115")])],"isStart":false});
            var sketch = newSketch(context, id + "F46", { "sketchPlane" : qUnion([Q0])});
            skCircle(sketch, "E116.0", {"center": v(-13, 35) * mm, "radius": 1.25 * mm});
            skLineSegment(sketch, "E117.rect.bottom", {"start": v(-17, 30) * mm, "end": v(-9, 30) * mm});
            skLineSegment(sketch, "E117.rect.top", {"start": v(-17, 40) * mm, "end": v(-9, 40) * mm});
            skLineSegment(sketch, "E117.rect.left", {"start": v(-17, 30) * mm, "end": v(-17, 40) * mm});
            skLineSegment(sketch, "E117.rect.right", {"start": v(-9, 30) * mm, "end": v(-9, 40) * mm});
            skSolve(sketch);
        }
        {
            var Q0;
            Q0=makeQuery(id+"F46.imprint","IMPRINT",FACE,{"disambiguationData":[TD([[makeQuery(id+"F46.imprint","IMPRINT",EDGE,{"derivedFrom":sQuery(id+"F46.wireOp",EDGE,"E116.0")}),-1.0]])]});
            var Q1;
            {var subQ1=sQuery(id+"F46.wireOp",EDGE,"E117.rect.left");var subQ3=sQuery(id+"F46.wireOp",EDGE,"E117.rect.top");var subQ5=makeQuery(id+"F46.imprint","INTERSECT",VERTEX,{"derivedFrom":[subQ3,subQ1]});Q1=makeQuery(id+"F46.imprint","IMPRINT",FACE,{"disambiguationData":[TD([[makeQuery(id+"F46.imprint","IMPRINT",EDGE,{"disambiguationData":[TD([[subQ5,-1.0]])],"derivedFrom":subQ3}),-1.0]])]});}
            var Q2;
            Q2=makeQuery(id+"F46.imprint","IMPRINT",FACE,{"disambiguationData":[TD([[makeQuery(id+"F46.imprint","IMPRINT",EDGE,{"derivedFrom":sQuery(id+"F46.wireOp",EDGE,"E116.0")}),1.0]])]});
            extrude(context, id + "F47", {"entities" : qUnion([Q0, Q1, Q2]), "depth" : 9.5 * mm});
        }
        {
            var Q0;
            Q0=makeQuery(id+"F47.opExtrude","SWEPT_FACE",FACE,{"disambiguationData":[OSD([sQuery(id+"F46.wireOp",EDGE,"E117.rect.top")])]});
            var sketch = newSketch(context, id + "F48", { "sketchPlane" : qUnion([Q0])});
            skLineSegment(sketch, "E118", {"start": v(53, -13) * mm, "end": v(58.5, -13) * mm, "construction": true});
            skCircle(sketch, "E119", {"center": v(58.5, -13) * mm, "radius": 2 * mm});
            skSolve(sketch);
        }
        {
            var Q0;
            Q0=makeQuery(id+"F48.imprint","IMPRINT",FACE,{"disambiguationData":[TD([[makeQuery(id+"F48.imprint","IMPRINT",EDGE,{"derivedFrom":sQuery(id+"F48.wireOp",EDGE,"E119")}),1.0]])]});
            extrude(context, id + "F49", {"entities" : qUnion([Q0]), "operationType" : NewBodyOperationType.REMOVE, "oppositeDirection" : true, "depth" : 10 * mm});
        }
        {
            var Q0;
            Q0=makeQuery(id+"F47.opExtrude","CAP_EDGE",EDGE,{"disambiguationData":[OSD([sQuery(id+"F46.wireOp",EDGE,"E117.rect.left")])],"isStart":false});
            var Q1;
            Q1=makeQuery(id+"F47.opExtrude","CAP_EDGE",EDGE,{"disambiguationData":[OSD([sQuery(id+"F46.wireOp",EDGE,"E117.rect.right")])],"isStart":false});
            fillet(context, id + "F50", {"entities" : qUnion([Q0, Q1]), "radius" : 4 * mm, "tangentPropagation" : true, "allowEdgeOverflow" : false});
        }
        {
            var Q0;
            Q0=makeQuery(id+"F46.imprint","IMPRINT",FACE,{"disambiguationData":[TD([[makeQuery(id+"F46.imprint","IMPRINT",EDGE,{"derivedFrom":sQuery(id+"F46.wireOp",EDGE,"E116.0")}),1.0]])]});
            extrude(context, id + "F51", {"entities" : qUnion([Q0]), "operationType" : NewBodyOperationType.REMOVE, "depth" : 5.5 * mm});
        }
        {
            var Q0;
            Q0=qCreatedBy(id+"F43.planeOp",FACE);
            var sketch = newSketch(context, id + "F52", { "sketchPlane" : qUnion([Q0])});
            skCircle(sketch, "E120.0", {"center": v(109, 127.5) * mm, "radius": 1.5 * mm});
            skLineSegment(sketch, "E121.rect.bottom", {"start": v(106, 124.5) * mm, "end": v(112, 124.5) * mm});
            skLineSegment(sketch, "E121.rect.top", {"start": v(106, 130.5) * mm, "end": v(112, 130.5) * mm});
            skLineSegment(sketch, "E121.rect.left", {"start": v(106, 124.5) * mm, "end": v(106, 130.5) * mm});
            skLineSegment(sketch, "E121.rect.right", {"start": v(112, 124.5) * mm, "end": v(112, 130.5) * mm});
            skSolve(sketch);
        }
        {
            var Q0;
            Q0=makeQuery(id+"F52.imprint","IMPRINT",FACE,{"disambiguationData":[TD([[makeQuery(id+"F52.imprint","IMPRINT",EDGE,{"derivedFrom":sQuery(id+"F52.wireOp",EDGE,"E120.0")}),1.0]])]});
            extrude(context, id + "F53", {"entities" : qUnion([Q0]), "oppositeDirection" : true, "depth" : 4 * mm});
        }
        {
            var Q0;
            Q0=makeQuery(id+"F52.imprint","IMPRINT",FACE,{"disambiguationData":[TD([[makeQuery(id+"F52.imprint","IMPRINT",EDGE,{"derivedFrom":sQuery(id+"F52.wireOp",EDGE,"E120.0")}),-1.0]])]});
            var Q1;
            Q1=makeQuery(id+"F52.imprint","IMPRINT",FACE,{"disambiguationData":[TD([[makeQuery(id+"F52.imprint","IMPRINT",EDGE,{"derivedFrom":sQuery(id+"F52.wireOp",EDGE,"E120.0")}),1.0]])]});
            extrude(context, id + "F54", {"entities" : qUnion([Q0, Q1]), "operationType" : NewBodyOperationType.ADD, "depth" : 10 * mm});
        }
        {
            var Q0;
            Q0=makeQuery(id+"F54.opExtrude","SWEPT_FACE",FACE,{"disambiguationData":[OSD([sQuery(id+"F52.wireOp",EDGE,"E121.rect.top")])]});
            var sketch = newSketch(context, id + "F55", { "sketchPlane" : qUnion([Q0])});
            skLineSegment(sketch, "E122", {"start": v(51.5, 109) * mm, "end": v(58.5, 109) * mm, "construction": true});
            skCircle(sketch, "E123", {"center": v(58.5, 109) * mm, "radius": 2 * mm});
            skSolve(sketch);
        }
        {
            var Q0;
            Q0=makeQuery(id+"F55.imprint","IMPRINT",FACE,{"disambiguationData":[TD([[makeQuery(id+"F55.imprint","IMPRINT",EDGE,{"derivedFrom":sQuery(id+"F55.wireOp",EDGE,"E123")}),1.0]])]});
            extrude(context, id + "F56", {"entities" : qUnion([Q0]), "operationType" : NewBodyOperationType.REMOVE, "oppositeDirection" : true, "depth" : 6 * mm});
        }
        {
            var Q0;
            Q0=makeQuery(id+"F54.opExtrude","CAP_EDGE",EDGE,{"disambiguationData":[OSD([sQuery(id+"F52.wireOp",EDGE,"E121.rect.left")])],"isStart":false});
            var Q1;
            Q1=makeQuery(id+"F54.opExtrude","CAP_EDGE",EDGE,{"disambiguationData":[OSD([sQuery(id+"F52.wireOp",EDGE,"E121.rect.right")])],"isStart":false});
            fillet(context, id + "F57", {"entities" : qUnion([Q0, Q1]), "radius" : 3 * mm, "tangentPropagation" : true, "allowEdgeOverflow" : false});
        }
        {
            var Q0;
            Q0=makeQuery(id+"F1.opExtrude","CAP_FACE",FACE,{"disambiguationData":[OSD([sQuery(id+"F0.wireOp",EDGE,"E0"),sQuery(id+"F0.wireOp",EDGE,"E1"),sQuery(id+"F0.wireOp",EDGE,"E2"),sQuery(id+"F0.wireOp",EDGE,"E3"),sQuery(id+"F0.wireOp",EDGE,"E4"),sQuery(id+"F0.wireOp",EDGE,"E15"),sQuery(id+"F0.wireOp",EDGE,"E17"),sQuery(id+"F0.wireOp",EDGE,"E18"),sQuery(id+"F0.wireOp",EDGE,"E19"),sQuery(id+"F0.wireOp",EDGE,"E20"),sQuery(id+"F0.wireOp",EDGE,"E21"),sQuery(id+"F0.wireOp",EDGE,"E22"),sQuery(id+"F0.wireOp",EDGE,"E23"),sQuery(id+"F0.wireOp",EDGE,"E24"),sQuery(id+"F0.wireOp",EDGE,"E25.0.1.0"),sQuery(id+"F0.wireOp",EDGE,"E25.0.2.0"),sQuery(id+"F0.wireOp",EDGE,"E26.0.1.0"),sQuery(id+"F0.wireOp",EDGE,"E26.0.2.0"),sQuery(id+"F0.wireOp",EDGE,"E28"),sQuery(id+"F0.wireOp",EDGE,"E30"),sQuery(id+"F0.wireOp",EDGE,"E32"),sQuery(id+"F0.wireOp",EDGE,"E33.1.0"),sQuery(id+"F0.wireOp",EDGE,"E33.2.0"),sQuery(id+"F0.wireOp",EDGE,"E33.3.0"),sQuery(id+"F0.wireOp",EDGE,"E35"),sQuery(id+"F0.wireOp",EDGE,"E36.1.0"),sQuery(id+"F0.wireOp",EDGE,"E36.2.0"),sQuery(id+"F0.wireOp",EDGE,"E36.3.0"),sQuery(id+"F0.wireOp",EDGE,"E38"),sQuery(id+"F0.wireOp",EDGE,"E39.1.0"),sQuery(id+"F0.wireOp",EDGE,"E39.2.0"),sQuery(id+"F0.wireOp",EDGE,"E39.3.0"),sQuery(id+"F0.wireOp",EDGE,"E40"),sQuery(id+"F0.wireOp",EDGE,"E41"),sQuery(id+"F0.wireOp",EDGE,"E43"),sQuery(id+"F0.wireOp",EDGE,"E44.0.1.0"),sQuery(id+"F0.wireOp",EDGE,"E44.0.2.0"),sQuery(id+"F0.wireOp",EDGE,"E44.1.0.0"),sQuery(id+"F0.wireOp",EDGE,"E44.1.1.0"),sQuery(id+"F0.wireOp",EDGE,"E44.1.2.0"),sQuery(id+"F0.wireOp",EDGE,"E44.2.0.0"),sQuery(id+"F0.wireOp",EDGE,"E44.2.1.0"),sQuery(id+"F0.wireOp",EDGE,"E44.2.2.0"),sQuery(id+"F0.wireOp",EDGE,"E46"),sQuery(id+"F0.wireOp",EDGE,"E47.0.1.0"),sQuery(id+"F0.wireOp",EDGE,"E47.0.2.0"),sQuery(id+"F0.wireOp",EDGE,"E48.filletArc"),sQuery(id+"F0.wireOp",EDGE,"E49.1.0"),sQuery(id+"F0.wireOp",EDGE,"E49.2.0")])],"isStart":true});
            var sketch = newSketch(context, id + "F58", { "sketchPlane" : qUnion([Q0])});
            skCircle(sketch, "E124.0", {"center": v(-116, 102) * mm, "radius": 1.25 * mm});
            skCircle(sketch, "E125", {"center": v(-116, 102) * mm, "radius": 3 * mm});
            skSolve(sketch);
        }
        {
            var Q0;
            Q0=makeQuery(id+"F58.imprint","IMPRINT",FACE,{"disambiguationData":[TD([[makeQuery(id+"F58.imprint","IMPRINT",EDGE,{"derivedFrom":sQuery(id+"F58.wireOp",EDGE,"E124.0")}),-1.0]])]});
            extrude(context, id + "F59", {"entities" : qUnion([Q0]), "oppositeDirection" : true, "depth" : 5 * mm});
        }
        {
            var Q0;
            Q0=makeQuery(id+"F58.imprint","IMPRINT",FACE,{"disambiguationData":[TD([[makeQuery(id+"F58.imprint","IMPRINT",EDGE,{"derivedFrom":sQuery(id+"F58.wireOp",EDGE,"E124.0")}),-1.0]])]});
            extrude(context, id + "F60", {"entities" : qUnion([Q0]), "operationType" : NewBodyOperationType.ADD, "depth" : 13 * mm});
        }
        {
            var Q0;
            Q0=makeQuery(id+"F58.imprint","IMPRINT",FACE,{"disambiguationData":[TD([[makeQuery(id+"F58.imprint","IMPRINT",EDGE,{"derivedFrom":sQuery(id+"F58.wireOp",EDGE,"E124.0")}),1.0]])]});
            extrude(context, id + "F61", {"entities" : qUnion([Q0]), "operationType" : NewBodyOperationType.ADD, "depth" : 8 * mm});
        }
        {
            var Q0;
            Q0=makeQuery(id+"F61.opExtrude","CAP_FACE",FACE,{"disambiguationData":[OSD([sQuery(id+"F58.wireOp",EDGE,"E124.0"),sQuery(id+"F58.wireOp",EDGE,"E125")])],"isStart":false});
            var sketch = newSketch(context, id + "F62", { "sketchPlane" : qUnion([Q0])});
            skCircle(sketch, "E126.0", {"center": v(-116, 102) * mm, "radius": 3 * mm});
            skCircle(sketch, "E126.1", {"center": v(-116, 102) * mm, "radius": 1.25 * mm});
            skLineSegment(sketch, "E127.bottom", {"start": v(-116, 103.5) * mm, "end": v(-127.5, 103.5) * mm});
            skLineSegment(sketch, "E127.top", {"start": v(-116, 100.5) * mm, "end": v(-127.5, 100.5) * mm});
            skLineSegment(sketch, "E127.left", {"start": v(-116, 103.5) * mm, "end": v(-116, 100.5) * mm});
            skLineSegment(sketch, "E127.right", {"start": v(-127.5, 103.5) * mm, "end": v(-127.5, 100.5) * mm});
            skArc(sketch, "E128", {"start": v(-127.5, 103.5) * mm, "mid": v(-129, 102) * mm, "end": v(-127.5, 100.5) * mm});
            skSolve(sketch);
        }
        {
            var Q0;
            {var subQ3=sQuery(id+"F62.wireOp",EDGE,"E127.right");Q0=makeQuery(id+"F62.imprint","IMPRINT",FACE,{"disambiguationData":[TD([[makeQuery(id+"F62.imprint","IMPRINT",EDGE,{"derivedFrom":subQ3}),1.0]])]});}
            var Q1;
            Q1=makeQuery(id+"F62.imprint","IMPRINT",FACE,{"disambiguationData":[TD([[makeQuery(id+"F62.imprint","IMPRINT",EDGE,{"derivedFrom":sQuery(id+"F62.wireOp",EDGE,"E127.right")}),-1.0]])]});
            var Q2;
            {var subQ6=sQuery(id+"F62.wireOp",EDGE,"E127.bottom");var subQ8=sQuery(id+"F62.wireOp",EDGE,"E126.0");var subQ10=makeQuery(id+"F62.imprint","INTERSECT",VERTEX,{"derivedFrom":[subQ8,subQ6]});Q2=makeQuery(id+"F62.imprint","IMPRINT",FACE,{"disambiguationData":[TD([[makeQuery(id+"F62.imprint","IMPRINT",EDGE,{"disambiguationData":[TD([[subQ10,-1.0]])],"derivedFrom":subQ8}),1.0]])]});}
            var Q3;
            {var subQ6=sQuery(id+"F62.wireOp",EDGE,"E127.bottom");var subQ8=sQuery(id+"F62.wireOp",EDGE,"E126.0");var subQ10=makeQuery(id+"F62.imprint","INTERSECT",VERTEX,{"derivedFrom":[subQ8,subQ6]});Q3=makeQuery(id+"F62.imprint","IMPRINT",FACE,{"disambiguationData":[TD([[makeQuery(id+"F62.imprint","IMPRINT",EDGE,{"disambiguationData":[TD([[subQ10,1.0]])],"derivedFrom":subQ8}),1.0]])]});}
            extrude(context, id + "F63", {"entities" : qUnion([Q0, Q1, Q2, Q3]), "depth" : 1.5 * mm});
        }
        {
            var Q0;
            Q0=makeQuery(id+"F1.opExtrude","SWEPT_FACE",FACE,{"disambiguationData":[OSD([sQuery(id+"F0.wireOp",EDGE,"E2")])]});
            var sketch = newSketch(context, id + "F64", { "sketchPlane" : qUnion([Q0])});
            skCircle(sketch, "E129.0", {"center": v(2.5, 90.7) * mm, "radius": 1.5 * mm});
            skCircle(sketch, "E130", {"center": v(2.5, 90.7) * mm, "radius": 2.25 * mm});
            skCircle(sketch, "E131", {"center": v(2.5, 90.7) * mm, "radius": 1 * mm});
            skCircle(sketch, "E132.cCircle", {"center": v(2.5, 90.7) * mm, "radius": 1.25 * mm, "construction": true});
            skLineSegment(sketch, "E132.0", {"start": v(1.25, 89.98) * mm, "end": v(1.25, 91.42) * mm});
            skLineSegment(sketch, "E132.1", {"start": v(1.25, 91.42) * mm, "end": v(2.5, 92.14) * mm});
            skLineSegment(sketch, "E132.2", {"start": v(2.5, 92.14) * mm, "end": v(3.75, 91.42) * mm});
            skLineSegment(sketch, "E132.3", {"start": v(3.75, 91.42) * mm, "end": v(3.75, 89.98) * mm});
            skLineSegment(sketch, "E132.4", {"start": v(3.75, 89.98) * mm, "end": v(2.5, 89.26) * mm});
            skLineSegment(sketch, "E132.5", {"start": v(2.5, 89.26) * mm, "end": v(1.25, 89.98) * mm});
            skPoint(sketch, "E132.0.midPoint", {"position": v(1.25, 90.7) * mm});
            skSolve(sketch);
        }
        {
            var Q0;
            Q0=makeQuery(id+"F64.imprint","IMPRINT",FACE,{"disambiguationData":[TD([[makeQuery(id+"F64.imprint","IMPRINT",EDGE,{"derivedFrom":sQuery(id+"F64.wireOp",EDGE,"E131")}),-1.0]])]});
            var Q1;
            Q1=makeQuery(id+"F64.imprint","IMPRINT",FACE,{"disambiguationData":[TD([[makeQuery(id+"F64.imprint","IMPRINT",EDGE,{"derivedFrom":sQuery(id+"F64.wireOp",EDGE,"E129.0")}),1.0]])]});
            extrude(context, id + "F65", {"entities" : qUnion([Q0, Q1]), "oppositeDirection" : true, "depth" : 5 * mm});
        }
        {
            var Q0;
            Q0=makeQuery(id+"F64.imprint","IMPRINT",FACE,{"disambiguationData":[TD([[makeQuery(id+"F64.imprint","IMPRINT",EDGE,{"derivedFrom":sQuery(id+"F64.wireOp",EDGE,"E129.0")}),-1.0]])]});
            var Q1;
            Q1=makeQuery(id+"F64.imprint","IMPRINT",FACE,{"disambiguationData":[TD([[makeQuery(id+"F64.imprint","IMPRINT",EDGE,{"derivedFrom":sQuery(id+"F64.wireOp",EDGE,"E131")}),-1.0]])]});
            var Q2;
            Q2=makeQuery(id+"F64.imprint","IMPRINT",FACE,{"disambiguationData":[TD([[makeQuery(id+"F64.imprint","IMPRINT",EDGE,{"derivedFrom":sQuery(id+"F64.wireOp",EDGE,"E131")}),1.0]])]});
            var Q3;
            Q3=makeQuery(id+"F64.imprint","IMPRINT",FACE,{"disambiguationData":[TD([[makeQuery(id+"F64.imprint","IMPRINT",EDGE,{"derivedFrom":sQuery(id+"F64.wireOp",EDGE,"E129.0")}),1.0]])]});
            extrude(context, id + "F66", {"entities" : qUnion([Q0, Q1, Q2, Q3]), "operationType" : NewBodyOperationType.ADD, "depth" : 3 * mm});
        }
        {
            var Q0;
            Q0=makeQuery(id+"F66.opExtrude","CAP_FACE",FACE,{"disambiguationData":[OSD([sQuery(id+"F64.wireOp",EDGE,"E130")])],"isStart":false});
            var sketch = newSketch(context, id + "F67", { "sketchPlane" : qUnion([Q0])});
            skLineSegment(sketch, "E133.0", {"start": v(2.5, 92.14) * mm, "end": v(3.75, 91.42) * mm});
            skLineSegment(sketch, "E133.1", {"start": v(1.25, 91.42) * mm, "end": v(2.5, 92.14) * mm});
            skLineSegment(sketch, "E133.2", {"start": v(1.25, 89.98) * mm, "end": v(1.25, 91.42) * mm});
            skLineSegment(sketch, "E133.3", {"start": v(2.5, 89.26) * mm, "end": v(1.25, 89.98) * mm});
            skLineSegment(sketch, "E133.4", {"start": v(3.75, 89.98) * mm, "end": v(2.5, 89.26) * mm});
            skLineSegment(sketch, "E133.5", {"start": v(3.75, 91.42) * mm, "end": v(3.75, 89.98) * mm});
            skSolve(sketch);
        }
        {
            var Q0;
            Q0=makeQuery(id+"F67.imprint","IMPRINT",FACE,{"disambiguationData":[TD([[makeQuery(id+"F67.imprint","IMPRINT",EDGE,{"derivedFrom":sQuery(id+"F67.wireOp",EDGE,"E133.0")}),-1.0]])]});
            extrude(context, id + "F68", {"entities" : qUnion([Q0]), "operationType" : NewBodyOperationType.REMOVE, "oppositeDirection" : true, "depth" : 1 * mm});
        }
        {
            var Q0;
            Q0=makeQuery(id+"F66.opExtrude","CAP_EDGE",EDGE,{"disambiguationData":[OSD([sQuery(id+"F64.wireOp",EDGE,"E130")])],"isStart":false});
            chamfer(context, id + "F69", {"entities" : qUnion([Q0]), "width" : 0.2 * mm, "tangentPropagation" : true});
        }
        {
            var Q0;
            Q0=makeQuery(id+"F66.boolean.opBoolean","SPLIT",FACE,{"disambiguationData":[TD([makeQuery(id+"F65.opExtrude","SWEPT_FACE",FACE,{"disambiguationData":[OSD([sQuery(id+"F64.wireOp",EDGE,"E131")])]})])],"derivedFrom":makeQuery(id+"F66.opExtrude","CAP_FACE",FACE,{"disambiguationData":[OSD([sQuery(id+"F64.wireOp",EDGE,"E130")])],"isStart":true})});
            extrude(context, id + "F70", {"entities" : qUnion([Q0]), "operationType" : NewBodyOperationType.REMOVE, "oppositeDirection" : true, "depth" : 1 * mm});
        }
        {
            var Q0;
            Q0=makeQuery(id+"F65.opExtrude","CAP_EDGE",EDGE,{"disambiguationData":[OSD([sQuery(id+"F64.wireOp",EDGE,"E129.0")])],"isStart":false});
            chamfer(context, id + "F71", {"entities" : qUnion([Q0]), "width" : 0.2 * mm, "tangentPropagation" : true});
        }
        {
            var Q0;
            Q0=makeQuery(id+"F1.opExtrude","SWEPT_FACE",FACE,{"disambiguationData":[OSD([sQuery(id+"F0.wireOp",EDGE,"E2")])]});
            var sketch = newSketch(context, id + "F72", { "sketchPlane" : qUnion([Q0])});
            skCircle(sketch, "E134.0", {"center": v(2.5, 24) * mm, "radius": 1.5 * mm});
            skCircle(sketch, "E135", {"center": v(2.5, 24) * mm, "radius": 1 * mm});
            skSolve(sketch);
        }
        {
            var Q0;
            Q0=makeQuery(id+"F72.imprint","IMPRINT",FACE,{"disambiguationData":[TD([[makeQuery(id+"F72.imprint","IMPRINT",EDGE,{"derivedFrom":sQuery(id+"F72.wireOp",EDGE,"E134.0")}),1.0]])]});
            extrude(context, id + "F73", {"entities" : qUnion([Q0]), "depth" : 7 * mm});
        }
        {
            var Q0;
            Q0=makeQuery(id+"F73.opExtrude","CAP_FACE",FACE,{"disambiguationData":[OSD([sQuery(id+"F72.wireOp",EDGE,"E134.0"),sQuery(id+"F72.wireOp",EDGE,"E135")])],"isStart":false});
            var sketch = newSketch(context, id + "F74", { "sketchPlane" : qUnion([Q0])});
            skCircle(sketch, "E136", {"center": v(2.5, 24) * mm, "radius": 2.25 * mm});
            skSolve(sketch);
        }
        {
            var Q0;
            Q0=makeQuery(id+"F74.imprint","IMPRINT",FACE,{"disambiguationData":[TD([[makeQuery(id+"F74.imprint","IMPRINT",EDGE,{"derivedFrom":sQuery(id+"F74.wireOp",EDGE,"E136")}),1.0]])]});
            var Q1;
            Q1=makeQuery(id+"F74.imprint","IMPRINT",FACE,{"disambiguationData":[TD([[makeQuery(id+"F74.imprint","IMPRINT",EDGE,{"derivedFrom":makeQuery(id+"F73.opExtrude","CAP_EDGE",EDGE,{"disambiguationData":[OSD([sQuery(id+"F72.wireOp",EDGE,"E134.0")])],"isStart":false})}),1.0]])]});
            var Q2;
            Q2=makeQuery(id+"F74.imprint","IMPRINT",FACE,{"disambiguationData":[TD([[makeQuery(id+"F74.imprint","IMPRINT",EDGE,{"derivedFrom":makeQuery(id+"F73.opExtrude","CAP_EDGE",EDGE,{"disambiguationData":[OSD([sQuery(id+"F72.wireOp",EDGE,"E135")])],"isStart":false})}),1.0]])]});
            extrude(context, id + "F75", {"entities" : qUnion([Q0, Q1, Q2]), "operationType" : NewBodyOperationType.ADD, "depth" : 3 * mm});
        }
        {
            var Q0;
            Q0=makeQuery(id+"F75.opExtrude","CAP_FACE",FACE,{"disambiguationData":[OSD([sQuery(id+"F74.wireOp",EDGE,"E136")])],"isStart":false});
            var sketch = newSketch(context, id + "F76", { "sketchPlane" : qUnion([Q0])});
            skCircle(sketch, "E137.cCircle", {"center": v(2.5, 24) * mm, "radius": 1.25 * mm, "construction": true});
            skLineSegment(sketch, "E137.0", {"start": v(1.25, 23.28) * mm, "end": v(1.25, 24.72) * mm});
            skLineSegment(sketch, "E137.1", {"start": v(1.25, 24.72) * mm, "end": v(2.5, 25.44) * mm});
            skLineSegment(sketch, "E137.2", {"start": v(2.5, 25.44) * mm, "end": v(3.75, 24.72) * mm});
            skLineSegment(sketch, "E137.3", {"start": v(3.75, 24.72) * mm, "end": v(3.75, 23.28) * mm});
            skLineSegment(sketch, "E137.4", {"start": v(3.75, 23.28) * mm, "end": v(2.5, 22.56) * mm});
            skLineSegment(sketch, "E137.5", {"start": v(2.5, 22.56) * mm, "end": v(1.25, 23.28) * mm});
            skPoint(sketch, "E137.0.midPoint", {"position": v(1.25, 24) * mm});
            skSolve(sketch);
        }
        {
            var Q0;
            Q0=makeQuery(id+"F76.imprint","IMPRINT",FACE,{"disambiguationData":[TD([[makeQuery(id+"F76.imprint","IMPRINT",EDGE,{"derivedFrom":sQuery(id+"F76.wireOp",EDGE,"E137.0")}),-1.0]])]});
            extrude(context, id + "F77", {"entities" : qUnion([Q0]), "operationType" : NewBodyOperationType.REMOVE, "oppositeDirection" : true, "depth" : 1 * mm});
        }
        {
            var Q0;
            Q0=makeQuery(id+"F75.opExtrude","CAP_EDGE",EDGE,{"disambiguationData":[OSD([sQuery(id+"F74.wireOp",EDGE,"E136")])],"isStart":false});
            var Q1;
            Q1=makeQuery(id+"F73.opExtrude","CAP_EDGE",EDGE,{"disambiguationData":[OSD([sQuery(id+"F72.wireOp",EDGE,"E134.0")])],"isStart":true});
            chamfer(context, id + "F78", {"entities" : qUnion([Q0, Q1]), "width" : 0.2 * mm, "tangentPropagation" : true});
        }
        {
            var Q0;
            Q0=makeQuery(id+"F1.opExtrude","SWEPT_FACE",FACE,{"disambiguationData":[OSD([sQuery(id+"F0.wireOp",EDGE,"E3")])]});
            var sketch = newSketch(context, id + "F79", { "sketchPlane" : qUnion([Q0])});
            skCircle(sketch, "E138.0", {"center": v(-2.5, 70.4) * mm, "radius": 1.5 * mm});
            skCircle(sketch, "E139", {"center": v(-2.5, 70.4) * mm, "radius": 1 * mm});
            skSolve(sketch);
        }
        {
            var Q0;
            Q0=makeQuery(id+"F79.imprint","IMPRINT",FACE,{"disambiguationData":[TD([[makeQuery(id+"F79.imprint","IMPRINT",EDGE,{"derivedFrom":sQuery(id+"F79.wireOp",EDGE,"E138.0")}),1.0]])]});
            extrude(context, id + "F80", {"entities" : qUnion([Q0]), "depth" : 5 * mm});
        }
        {
            var Q0;
            Q0=makeQuery(id+"F80.opExtrude","CAP_FACE",FACE,{"disambiguationData":[OSD([sQuery(id+"F79.wireOp",EDGE,"E138.0"),sQuery(id+"F79.wireOp",EDGE,"E139")])],"isStart":false});
            var sketch = newSketch(context, id + "F81", { "sketchPlane" : qUnion([Q0])});
            skCircle(sketch, "E140", {"center": v(-2.5, 70.4) * mm, "radius": 2.25 * mm});
            skSolve(sketch);
        }
        {
            var Q0;
            Q0=makeQuery(id+"F81.imprint","IMPRINT",FACE,{"disambiguationData":[TD([[makeQuery(id+"F81.imprint","IMPRINT",EDGE,{"derivedFrom":makeQuery(id+"F80.opExtrude","CAP_EDGE",EDGE,{"disambiguationData":[OSD([sQuery(id+"F79.wireOp",EDGE,"E139")])],"isStart":false})}),1.0]])]});
            extrude(context, id + "F82", {"entities" : qUnion([Q0]), "operationType" : NewBodyOperationType.ADD, "oppositeDirection" : true, "depth" : 1 * mm});
        }
        {
            var Q0;
            Q0=makeQuery(id+"F81.imprint","IMPRINT",FACE,{"disambiguationData":[TD([[makeQuery(id+"F81.imprint","IMPRINT",EDGE,{"derivedFrom":sQuery(id+"F81.wireOp",EDGE,"E140")}),1.0]])]});
            var Q1;
            Q1=makeQuery(id+"F81.imprint","IMPRINT",FACE,{"disambiguationData":[TD([[makeQuery(id+"F81.imprint","IMPRINT",EDGE,{"derivedFrom":makeQuery(id+"F80.opExtrude","CAP_EDGE",EDGE,{"disambiguationData":[OSD([sQuery(id+"F79.wireOp",EDGE,"E138.0")])],"isStart":false})}),1.0]])]});
            var Q2;
            Q2=makeQuery(id+"F81.imprint","IMPRINT",FACE,{"disambiguationData":[TD([[makeQuery(id+"F81.imprint","IMPRINT",EDGE,{"derivedFrom":makeQuery(id+"F80.opExtrude","CAP_EDGE",EDGE,{"disambiguationData":[OSD([sQuery(id+"F79.wireOp",EDGE,"E139")])],"isStart":false})}),1.0]])]});
            extrude(context, id + "F83", {"entities" : qUnion([Q0, Q1, Q2]), "operationType" : NewBodyOperationType.ADD, "depth" : 2 * mm});
        }
        {
            var Q0;
            Q0=makeQuery(id+"F83.opExtrude","CAP_FACE",FACE,{"disambiguationData":[OSD([sQuery(id+"F81.wireOp",EDGE,"E140")])],"isStart":false});
            var sketch = newSketch(context, id + "F84", { "sketchPlane" : qUnion([Q0])});
            skCircle(sketch, "E141.cCircle", {"center": v(-2.5, 70.4) * mm, "radius": 1.25 * mm, "construction": true});
            skLineSegment(sketch, "E141.0", {"start": v(-3.75, 69.68) * mm, "end": v(-3.75, 71.12) * mm});
            skLineSegment(sketch, "E141.1", {"start": v(-3.75, 71.12) * mm, "end": v(-2.5, 71.84) * mm});
            skLineSegment(sketch, "E141.2", {"start": v(-2.5, 71.84) * mm, "end": v(-1.25, 71.12) * mm});
            skLineSegment(sketch, "E141.3", {"start": v(-1.25, 71.12) * mm, "end": v(-1.25, 69.68) * mm});
            skLineSegment(sketch, "E141.4", {"start": v(-1.25, 69.68) * mm, "end": v(-2.5, 68.96) * mm});
            skLineSegment(sketch, "E141.5", {"start": v(-2.5, 68.96) * mm, "end": v(-3.75, 69.68) * mm});
            skPoint(sketch, "E141.0.midPoint", {"position": v(-3.75, 70.4) * mm});
            skSolve(sketch);
        }
        {
            var Q0;
            Q0=makeQuery(id+"F84.imprint","IMPRINT",FACE,{"disambiguationData":[TD([[makeQuery(id+"F84.imprint","IMPRINT",EDGE,{"derivedFrom":sQuery(id+"F84.wireOp",EDGE,"E141.0")}),-1.0]])]});
            extrude(context, id + "F85", {"entities" : qUnion([Q0]), "operationType" : NewBodyOperationType.REMOVE, "oppositeDirection" : true, "depth" : 1 * mm});
        }
        {
            var Q0;
            Q0=makeQuery(id+"F80.opExtrude","CAP_EDGE",EDGE,{"disambiguationData":[OSD([sQuery(id+"F79.wireOp",EDGE,"E138.0")])],"isStart":true});
            var Q1;
            Q1=makeQuery(id+"F83.opExtrude","CAP_EDGE",EDGE,{"disambiguationData":[OSD([sQuery(id+"F81.wireOp",EDGE,"E140")])],"isStart":false});
            chamfer(context, id + "F86", {"entities" : qUnion([Q0, Q1]), "width" : 0.2 * mm, "tangentPropagation" : true});
        }
        {
            var Q0;
            Q0=makeQuery(id+"F16.opExtrude","SWEPT_FACE",FACE,{"disambiguationData":[OSD([sQuery(id+"F0.wireOp",EDGE,"E3")])]});
            var sketch = newSketch(context, id + "F87", { "sketchPlane" : qUnion([Q0])});
            skCircle(sketch, "E142.0", {"center": v(-2.5, 43) * mm, "radius": 1.5 * mm});
            skCircle(sketch, "E143", {"center": v(-2.5, 43) * mm, "radius": 1 * mm});
            skSolve(sketch);
        }
        {
            var Q0;
            Q0=makeQuery(id+"F87.imprint","IMPRINT",FACE,{"disambiguationData":[TD([[makeQuery(id+"F87.imprint","IMPRINT",EDGE,{"derivedFrom":sQuery(id+"F87.wireOp",EDGE,"E142.0")}),1.0]])]});
            extrude(context, id + "F88", {"entities" : qUnion([Q0]), "depth" : 3 * mm});
        }
        {
            var Q0;
            Q0=makeQuery(id+"F88.opExtrude","CAP_FACE",FACE,{"disambiguationData":[OSD([sQuery(id+"F87.wireOp",EDGE,"E142.0"),sQuery(id+"F87.wireOp",EDGE,"E143")])],"isStart":false});
            var sketch = newSketch(context, id + "F89", { "sketchPlane" : qUnion([Q0])});
            skCircle(sketch, "E144", {"center": v(-2.5, 43) * mm, "radius": 2.25 * mm});
            skSolve(sketch);
        }
        {
            var Q0;
            Q0=makeQuery(id+"F89.imprint","IMPRINT",FACE,{"disambiguationData":[TD([[makeQuery(id+"F89.imprint","IMPRINT",EDGE,{"derivedFrom":makeQuery(id+"F88.opExtrude","CAP_EDGE",EDGE,{"disambiguationData":[OSD([sQuery(id+"F87.wireOp",EDGE,"E143")])],"isStart":false})}),1.0]])]});
            extrude(context, id + "F90", {"entities" : qUnion([Q0]), "operationType" : NewBodyOperationType.ADD, "oppositeDirection" : true, "depth" : 1 * mm});
        }
        {
            var Q0;
            Q0=makeQuery(id+"F89.imprint","IMPRINT",FACE,{"disambiguationData":[TD([[makeQuery(id+"F89.imprint","IMPRINT",EDGE,{"derivedFrom":sQuery(id+"F89.wireOp",EDGE,"E144")}),1.0]])]});
            var Q1;
            Q1=makeQuery(id+"F89.imprint","IMPRINT",FACE,{"disambiguationData":[TD([[makeQuery(id+"F89.imprint","IMPRINT",EDGE,{"derivedFrom":makeQuery(id+"F88.opExtrude","CAP_EDGE",EDGE,{"disambiguationData":[OSD([sQuery(id+"F87.wireOp",EDGE,"E142.0")])],"isStart":false})}),1.0]])]});
            var Q2;
            Q2=makeQuery(id+"F89.imprint","IMPRINT",FACE,{"disambiguationData":[TD([[makeQuery(id+"F89.imprint","IMPRINT",EDGE,{"derivedFrom":makeQuery(id+"F88.opExtrude","CAP_EDGE",EDGE,{"disambiguationData":[OSD([sQuery(id+"F87.wireOp",EDGE,"E143")])],"isStart":false})}),1.0]])]});
            extrude(context, id + "F91", {"entities" : qUnion([Q0, Q1, Q2]), "operationType" : NewBodyOperationType.ADD, "depth" : 2 * mm});
        }
        {
            var Q0;
            Q0=makeQuery(id+"F91.opExtrude","CAP_FACE",FACE,{"disambiguationData":[OSD([sQuery(id+"F89.wireOp",EDGE,"E144")])],"isStart":false});
            var sketch = newSketch(context, id + "F92", { "sketchPlane" : qUnion([Q0])});
            skCircle(sketch, "E145.cCircle", {"center": v(-2.5, 43) * mm, "radius": 1.25 * mm, "construction": true});
            skLineSegment(sketch, "E145.0", {"start": v(-1.78, 41.75) * mm, "end": v(-3.22, 41.75) * mm});
            skLineSegment(sketch, "E145.1", {"start": v(-3.22, 41.75) * mm, "end": v(-3.94, 43) * mm});
            skLineSegment(sketch, "E145.2", {"start": v(-3.94, 43) * mm, "end": v(-3.22, 44.25) * mm});
            skLineSegment(sketch, "E145.3", {"start": v(-3.22, 44.25) * mm, "end": v(-1.78, 44.25) * mm});
            skLineSegment(sketch, "E145.4", {"start": v(-1.78, 44.25) * mm, "end": v(-1.06, 43) * mm});
            skLineSegment(sketch, "E145.5", {"start": v(-1.06, 43) * mm, "end": v(-1.78, 41.75) * mm});
            skPoint(sketch, "E145.0.midPoint", {"position": v(-2.5, 41.75) * mm});
            skSolve(sketch);
        }
        {
            var Q0;
            Q0=makeQuery(id+"F92.imprint","IMPRINT",FACE,{"disambiguationData":[TD([[makeQuery(id+"F92.imprint","IMPRINT",EDGE,{"derivedFrom":sQuery(id+"F92.wireOp",EDGE,"E145.0")}),-1.0]])]});
            extrude(context, id + "F93", {"entities" : qUnion([Q0]), "operationType" : NewBodyOperationType.REMOVE, "oppositeDirection" : true, "depth" : 1 * mm});
        }
        {
            var Q0;
            Q0=makeQuery(id+"F88.opExtrude","CAP_EDGE",EDGE,{"disambiguationData":[OSD([sQuery(id+"F87.wireOp",EDGE,"E142.0")])],"isStart":true});
            var Q1;
            Q1=makeQuery(id+"F91.opExtrude","CAP_EDGE",EDGE,{"disambiguationData":[OSD([sQuery(id+"F89.wireOp",EDGE,"E144")])],"isStart":false});
            chamfer(context, id + "F94", {"entities" : qUnion([Q0, Q1]), "width" : 0.2 * mm, "tangentPropagation" : true});
        }
    });
